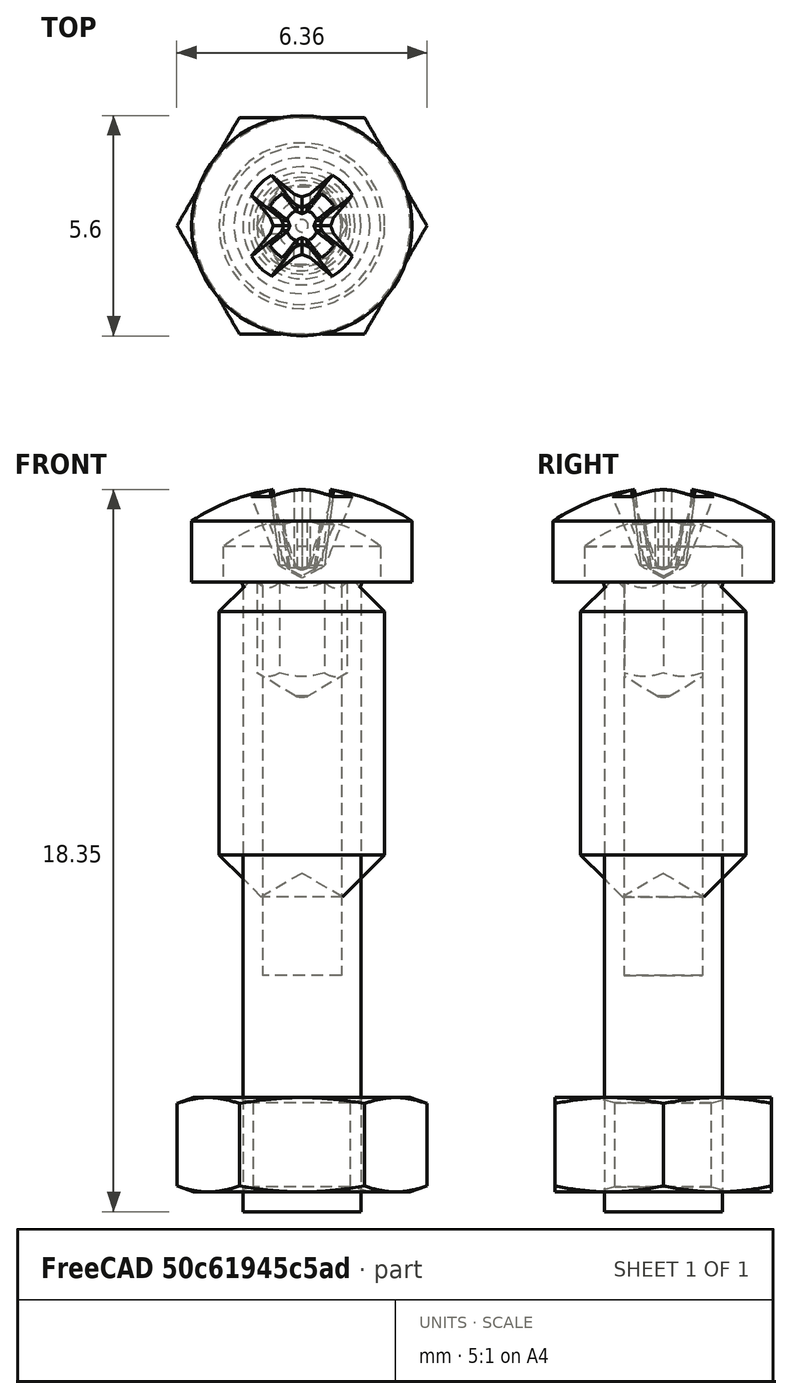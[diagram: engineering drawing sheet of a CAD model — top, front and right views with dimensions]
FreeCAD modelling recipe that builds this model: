
FCSTD DOCUMENT  (FreeCAD 0.19R24367 (Git))
Label: AssemblySteeringL
License: All rights reserved
LicenseURL: http://en.wikipedia.org/wiki/All_rights_reserved
objects: App::Link×16, PartDesign::CoordinateSystem×7, Part::FeaturePython×4, App::Part×4, App::DocumentObjectGroup×3, App::FeaturePython×1
note: 11 computed .brp shape members not serialized (recipe doc carries the construction recipe); baked Part::Feature solids carry a one-line shape summary decoded from their .brp
EXTERNAL_REF file=parts/SteeringKnuckle.FCStd obj=LCS_0001
EXTERNAL_REF file=parts/SteeringKnuckle.FCStd obj=SteeringKnuckleBottomL
EXTERNAL_REF file=parts/Servo.FCStd obj=LCS_1
EXTERNAL_REF file=parts/SteeringKnuckle.FCStd obj=LCS_2
EXTERNAL_REF file=parts/Servo.FCStd obj=Assembly
EXTERNAL_REF file=parts/SteeringKnuckle.FCStd obj=LCS_1
EXTERNAL_REF file=parts/SteeringKnuckle.FCStd obj=LCS_3
EXTERNAL_REF file=parts/SteeringKnuckle.FCStd obj=SteeringKnuckleTop
EXTERNAL_REF file=parts/SteeringKnuckle.FCStd obj=LCS_Screw01
EXTERNAL_REF file=parts/SteeringKnuckle.FCStd obj=LCS_Screw02
EXTERNAL_REF file=parts/SteeringKnuckle.FCStd obj=LCS_Screw03
EXTERNAL_REF file=parts/SteeringKnuckle.FCStd obj=LCS_Screw04
EXTERNAL_REF file=parts/Servo.FCStd obj=LCS_PlateTop
EXTERNAL_REF file=parts/ServoCoupler.FCStd obj=LCS_Bottom
EXTERNAL_REF file=parts/ServoCoupler.FCStd obj=ServoCoupler
EXTERNAL_REF file=parts/FixedRing.FCStd obj=LCS_Bottom
EXTERNAL_REF file=parts/ServoCoupler.FCStd obj=LCS_Top
EXTERNAL_REF file=parts/FixedRing.FCStd obj=FixedRing
EXTERNAL_REF file=parts/ServoCoupler.FCStd obj=LCS_Hole03
EXTERNAL_REF file=parts/ServoCoupler.FCStd obj=LCS_Hole04
EXTERNAL_REF file=parts/ServoCoupler.FCStd obj=LCS_Hole01
EXTERNAL_REF file=parts/ServoCoupler.FCStd obj=LCS_Hole02
EXTERNAL_REF file=parts/BallBearing.FCStd obj=LCS_Top
EXTERNAL_REF file=parts/SteeringKnuckle.FCStd obj=LCS_BallBearing
EXTERNAL_REF file=parts/BallBearing.FCStd obj=BallBearing
EXTERNAL_REF file=parts/Shaft.FCStd obj=LCS_0
EXTERNAL_REF file=parts/Shaft.FCStd obj=Shaft
EXTERNAL_REF file=parts/SteeringKnuckle.FCStd obj=LCS_SurfaceBearing
EXTERNAL_REF file=parts/SurfaceBearing.FCStd obj=LCS_Bottom
EXTERNAL_REF file=parts/SurfaceBearing.FCStd obj=Model

FEATURE [PartDesign::CoordinateSystem] LCS_Origin
  AttacherType = Attacher::AttachEngine3D
  MapMode = 2
  Support = -> [X_Axis]
FEATURE [App::FeaturePython] Variables  # WARN: FeaturePython — macro-defined, semantics opaque (R4)
  Type = App::PropertyContainer
FEATURE [App::DocumentObjectGroup] Constraints
FEATURE [App::DocumentObjectGroup] Configurations
FEATURE [App::Link] SteeringKnuckleBottomL
  AssemblyType = Part::Link
  AttachedBy = #LCS_0001
  AttachedTo = Parent Assembly#LCS_Origin
  LinkedObject = -> <external parts/SteeringKnuckle.FCStd>#SteeringKnuckleBottomL
  SolverId = Asm4EE
  expr: Placement = LCS_Origin.Placement * AttachmentOffset * SteeringKnuckle#LCS_0001.Placement ^ -1
FEATURE [App::Link] AssemblyServo
  AttachedBy = #LCS_1
  AttachedTo = SteeringKnuckleBottomL#LCS_2
  LinkPlacement = pos=(3e-16,0,-8.3) rot=(0,0,1;0rad)
  LinkedObject = -> <external parts/Servo.FCStd>#Assembly
  Placement = pos=(3e-16,0,-8.3) rot=(0,0,1;0rad)
  SolverId = Asm4EE
  expr: Placement = SteeringKnuckleBottomL.Placement * SteeringKnuckle#LCS_2.Placement * AttachmentOffset * Servo#LCS_1.Placement ^ -1
FEATURE [App::Link] SteeringKnuckleTop
  AssemblyType = Part::Link
  AttachedBy = #LCS_1
  AttachedTo = SteeringKnuckleBottomL#LCS_3
  AttachmentOffset = pos=(0,0,0) rot=(0,0,1;3.14159rad)
  LinkedObject = -> <external parts/SteeringKnuckle.FCStd>#SteeringKnuckleTop
  SolverId = Asm4EE
  expr: Placement = SteeringKnuckleBottomL.Placement * SteeringKnuckle#LCS_3.Placement * AttachmentOffset * SteeringKnuckle#LCS_1.Placement ^ -1
FEATURE [PartDesign::CoordinateSystem] LCS_0
  AttacherType = Attacher::AttachEngine3D
  MapMode = 2
  Support = -> [X_Axis001]
FEATURE [Part::FeaturePython] Screw  label="M3x16-Screw"  # Fasteners workbench fastener (typed FeaturePython)
  diameter = 4
  invert = false
  length = 7
  lengthCustom = 16
  matchOuter = false
  offset = 0
  thread = false
  type = 34
FEATURE [Part::FeaturePython] Nut  label="M3-Nut"  # Fasteners workbench fastener (typed FeaturePython)
  Placement = pos=(0,0,-15.5) rot=(0,0,1;0rad)
  diameter = 4
  invert = false
  matchOuter = false
  offset = 0
  thread = false
  type = 7
FEATURE [PartDesign::CoordinateSystem] LCS_Screw
  AttacherType = Attacher::AttachEngine3D
  MapMode = 45
  Placement = pos=(0,-2e-16,0) rot=(0,1,0;3.14159rad)
  Support = -> [Screw]
FEATURE [App::Part] Fastener
  Group = -> [LCS_0,Screw,Nut,LCS_Screw]
  Origin = -> Origin001
FEATURE [App::Link] Fastener001
  AssemblyType = Part::Link
  AttachedBy = #LCS_Screw
  AttachedTo = SteeringKnuckleBottomL#LCS_Screw01
  LinkPlacement = pos=(-19.799,19.799,-3) rot=(0,-1,0;3.14159rad)
  LinkedObject = -> Fastener
  Placement = pos=(-19.799,19.799,-3) rot=(0,-1,0;3.14159rad)
  SolverId = Asm4EE
  expr: Placement = SteeringKnuckleBottomL.Placement * SteeringKnuckle#LCS_Screw01.Placement * AttachmentOffset * LCS_Screw.Placement ^ -1
FEATURE [App::Link] Fastener002
  AssemblyType = Part::Link
  AttachedBy = #LCS_Screw
  AttachedTo = SteeringKnuckleBottomL#LCS_Screw02
  LinkPlacement = pos=(-19.799,-19.799,-3) rot=(0,-1,0;3.14159rad)
  LinkedObject = -> Fastener
  Placement = pos=(-19.799,-19.799,-3) rot=(0,-1,0;3.14159rad)
  SolverId = Asm4EE
  expr: Placement = SteeringKnuckleBottomL.Placement * SteeringKnuckle#LCS_Screw02.Placement * AttachmentOffset * LCS_Screw.Placement ^ -1
FEATURE [App::Link] Fastener003
  AssemblyType = Part::Link
  AttachedBy = #LCS_Screw
  AttachedTo = SteeringKnuckleBottomL#LCS_Screw03
  LinkPlacement = pos=(19.799,-19.799,-3) rot=(0,-1,0;3.14159rad)
  LinkedObject = -> Fastener
  Placement = pos=(19.799,-19.799,-3) rot=(0,-1,0;3.14159rad)
  SolverId = Asm4EE
  expr: Placement = SteeringKnuckleBottomL.Placement * SteeringKnuckle#LCS_Screw03.Placement * AttachmentOffset * LCS_Screw.Placement ^ -1
FEATURE [App::Link] Fastener004
  AssemblyType = Part::Link
  AttachedBy = #LCS_Screw
  AttachedTo = SteeringKnuckleBottomL#LCS_Screw04
  LinkPlacement = pos=(19.799,19.799,-3) rot=(0,-1,0;3.14159rad)
  LinkedObject = -> Fastener
  Placement = pos=(19.799,19.799,-3) rot=(0,-1,0;3.14159rad)
  SolverId = Asm4EE
  expr: Placement = SteeringKnuckleBottomL.Placement * SteeringKnuckle#LCS_Screw04.Placement * AttachmentOffset * LCS_Screw.Placement ^ -1
FEATURE [App::Link] ServoCoupler
  AssemblyType = Part::Link
  AttachedBy = #LCS_Bottom
  AttachedTo = AssemblyServo#LCS_PlateTop
  LinkPlacement = pos=(7e-16,1.9e-15,-18.3) rot=(0,-1,0;3.14159rad)
  LinkedObject = -> <external parts/ServoCoupler.FCStd>#ServoCoupler
  Placement = pos=(7e-16,1.9e-15,-18.3) rot=(0,-1,0;3.14159rad)
  SolverId = Asm4EE
  expr: Placement = AssemblyServo.Placement * Servo#LCS_PlateTop.Placement * AttachmentOffset * ServoCoupler#LCS_Bottom.Placement ^ -1
FEATURE [App::Link] FixedRing
  AssemblyType = Part::Link
  AttachedBy = #LCS_Bottom
  AttachedTo = ServoCoupler#LCS_Top
  AttachmentOffset = pos=(0,0,1) rot=(0,0,1;0rad)
  LinkPlacement = pos=(-1.33e-14,2.3e-15,-26.3) rot=(0.382683,-0.92388,0;3.14159rad)
  LinkedObject = -> <external parts/FixedRing.FCStd>#FixedRing
  Placement = pos=(-1.33e-14,2.3e-15,-26.3) rot=(0.382683,-0.92388,0;3.14159rad)
  SolverId = Asm4EE
  expr: Placement = ServoCoupler.Placement * ServoCoupler#LCS_Top.Placement * AttachmentOffset * FixedRing#LCS_Bottom.Placement ^ -1
FEATURE [PartDesign::CoordinateSystem] LCS_0001
  AttacherType = Attacher::AttachEngine3D
  MapMode = 2
  Support = -> [X_Axis002]
FEATURE [Part::FeaturePython] Screw002  label="#8x8-Screw"  # Fasteners workbench fastener (typed FeaturePython)
  diameter = 8
  invert = false
  length = 27
  lengthCustom = 8
  matchOuter = false
  offset = 0
  thread = false
  type = 10
FEATURE [PartDesign::CoordinateSystem] LCS_1
  AttacherType = Attacher::AttachEngine3D
  MapMode = 45
  Placement = pos=(6.4e-15,1e-16,0) rot=(0,1,0;3.14159rad)
  Support = -> [Screw002]
FEATURE [App::Part] Screw001
  Group = -> [LCS_0001,Screw002,LCS_1]
  Origin = -> Origin002
FEATURE [App::Link] Screw001001
  AssemblyType = Part::Link
  AttachedBy = #LCS_1
  AttachedTo = ServoCoupler#LCS_Hole03
  LinkPlacement = pos=(7.70335,7.70335,-29.1452) rot=(0.678591,0.281096,0.678601;3.6896rad)
  LinkedObject = -> Screw001
  Placement = pos=(7.70335,7.70335,-29.1452) rot=(0.678591,0.281096,0.678601;3.6896rad)
  SolverId = Asm4EE
  expr: Placement = ServoCoupler.Placement * ServoCoupler#LCS_Hole03.Placement * AttachmentOffset * LCS_1.Placement ^ -1
FEATURE [App::Link] Screw001002
  AssemblyType = Part::Link
  AttachedBy = #LCS_1
  AttachedTo = ServoCoupler#LCS_Hole04
  LinkPlacement = pos=(-7.70335,7.70335,-29.1452) rot=(0.35739,0.862858,0.35742;4.5654rad)
  LinkedObject = -> Screw001
  Placement = pos=(-7.70335,7.70335,-29.1452) rot=(0.35739,0.862858,0.35742;4.5654rad)
  SolverId = Asm4EE
  expr: Placement = ServoCoupler.Placement * ServoCoupler#LCS_Hole04.Placement * AttachmentOffset * LCS_1.Placement ^ -1
FEATURE [PartDesign::CoordinateSystem] LCS_0002
  AttacherType = Attacher::AttachEngine3D
  MapMode = 2
  Support = -> [X_Axis003]
FEATURE [Part::FeaturePython] Screw001004  label="M2x10-Screw"  # Fasteners workbench fastener (typed FeaturePython)
  diameter = 2
  invert = false
  length = 5
  lengthCustom = 10
  matchOuter = false
  offset = 0
  thread = false
  type = 34
FEATURE [PartDesign::CoordinateSystem] LCS_2
  AttacherType = Attacher::AttachEngine3D
  MapMode = 45
  Placement = pos=(-9e-16,-3e-16,0) rot=(0,1,0;3.14159rad)
  Support = -> [Screw001004]
FEATURE [App::Part] Screw001003  label="Screw002"
  Group = -> [LCS_0002,Screw001004,LCS_2]
  Origin = -> Origin003
FEATURE [App::DocumentObjectGroup] Parts
  Group = -> [Fastener,Screw001,Screw001003]
FEATURE [App::Link] Screw002001
  AssemblyType = Part::Link
  AttachedBy = #LCS_2
  AttachedTo = ServoCoupler#LCS_Hole01
  LinkPlacement = pos=(-7,-2.48e-14,-25.3) rot=(0,-1,0;3.14159rad)
  LinkedObject = -> Screw001003
  Placement = pos=(-7,-2.48e-14,-25.3) rot=(0,-1,0;3.14159rad)
  SolverId = Asm4EE
  expr: Placement = ServoCoupler.Placement * ServoCoupler#LCS_Hole01.Placement * AttachmentOffset * LCS_2.Placement ^ -1
FEATURE [App::Link] Screw002002
  AssemblyType = Part::Link
  AttachedBy = #LCS_2
  AttachedTo = ServoCoupler#LCS_Hole02
  LinkPlacement = pos=(7,2.92e-14,-25.3) rot=(0,-1,0;3.14159rad)
  LinkedObject = -> Screw001003
  Placement = pos=(7,2.92e-14,-25.3) rot=(0,-1,0;3.14159rad)
  SolverId = Asm4EE
  expr: Placement = ServoCoupler.Placement * ServoCoupler#LCS_Hole02.Placement * AttachmentOffset * LCS_2.Placement ^ -1
FEATURE [App::Link] BallBearing
  AssemblyType = Part::Link
  AttachedBy = #LCS_Top
  AttachedTo = SteeringKnuckleBottomL#LCS_BallBearing
  LinkPlacement = pos=(1.59e-14,2e-16,-48) rot=(0,1,0;3.14159rad)
  LinkedObject = -> <external parts/BallBearing.FCStd>#BallBearing
  Placement = pos=(1.59e-14,2e-16,-48) rot=(0,1,0;3.14159rad)
  SolverId = Asm4EE
  expr: Placement = SteeringKnuckleBottomL.Placement * SteeringKnuckle#LCS_BallBearing.Placement * AttachmentOffset * BallBearing#LCS_Top.Placement ^ -1
FEATURE [App::Link] Shaft
  AssemblyType = Part::Link
  AttachedBy = #LCS_0
  AttachedTo = FixedRing#LCS_Bottom
  LinkPlacement = pos=(-1.3e-14,2e-15,-26.3) rot=(0,-1,0;3.14159rad)
  LinkedObject = -> <external parts/Shaft.FCStd>#Shaft
  Placement = pos=(-1.3e-14,2e-15,-26.3) rot=(0,-1,0;3.14159rad)
  SolverId = Asm4EE
  expr: Placement = FixedRing.Placement * FixedRing#LCS_Bottom.Placement * AttachmentOffset * Shaft#LCS_0.Placement ^ -1
FEATURE [App::Link] SurfaceBearing
  AttachedBy = #LCS_Bottom
  AttachedTo = SteeringKnuckleBottomL#LCS_SurfaceBearing
  LinkPlacement = pos=(2.16e-14,0,-58) rot=(0,1,0;3.14159rad)
  LinkedObject = -> <external parts/SurfaceBearing.FCStd>#Model
  Placement = pos=(2.16e-14,0,-58) rot=(0,1,0;3.14159rad)
  SolverId = Asm4EE
  expr: Placement = SteeringKnuckleBottomL.Placement * SteeringKnuckle#LCS_SurfaceBearing.Placement * AttachmentOffset * SurfaceBearing#LCS_Bottom.Placement ^ -1
FEATURE [App::Part] Assembly  label="AssemblySteeringL"
  AssemblyType = Part::Link
  Group = -> [LCS_Origin,Variables,Constraints,Configurations,SteeringKnuckleBottomL,AssemblyServo,SteeringKnuckleTop,Fastener001,Fastener002,Fastener003,Fastener004,ServoCoupler,FixedRing,Screw001001,Screw001002,Screw002001,Screw002002,BallBearing,Shaft,SurfaceBearing]
  Origin = -> Origin
  Type = Assembly

RESOLVED EXTERNAL PARTS (link-assembly join: the EXTERNAL_REF files above that resolve inside this repo's crawl, each included once):
---- part parts/FixedRing.FCStd = doc fcstd_d6dc02ef2379 ----
FCSTD DOCUMENT  (FreeCAD 0.19R24367 (Git))
Label: FixedRing
License: All rights reserved
LicenseURL: http://en.wikipedia.org/wiki/All_rights_reserved
objects: PartDesign::CoordinateSystem×5, Sketcher::SketchObject×4, PartDesign::Chamfer×4, App::DocumentObjectGroup×3, PartDesign::Pocket×3, App::Part×2, App::FeaturePython×1, PartDesign::Pad×1, PartDesign::Body×1
note: 26 computed .brp shape members not serialized (recipe doc carries the construction recipe); baked Part::Feature solids carry a one-line shape summary decoded from their .brp

FEATURE [PartDesign::CoordinateSystem] LCS_Origin
  AttacherType = Attacher::AttachEngine3D
  MapMode = 2
  Support = -> [X_Axis]
FEATURE [App::FeaturePython] Variables  # WARN: FeaturePython — macro-defined, semantics opaque (R4)
  Type = App::PropertyContainer
FEATURE [App::DocumentObjectGroup] Constraints
FEATURE [App::DocumentObjectGroup] Configurations
FEATURE [App::Part] Assembly
  AssemblyType = Part::Link
  Group = -> [LCS_Origin,Variables,Constraints,Configurations]
  Origin = -> Origin
  Type = Assembly
FEATURE [PartDesign::CoordinateSystem] LCS_0
  AttacherType = Attacher::AttachEngine3D
  MapMode = 2
  Support = -> [X_Axis001]
FEATURE [PartDesign::CoordinateSystem] LCS_0001
  AttacherType = Attacher::AttachEngine3D
  MapMode = 2
  Support = -> [X_Axis002]
FEATURE [Sketcher::SketchObject] Sketch
  FullyConstrained = true
  MapMode = 5
  Support = -> [XY_Plane002]
  sketch-geometry (1):
    g0: Circle CenterX=0 CenterY=0 CenterZ=0 NormalX=0 NormalY=0 NormalZ=1 AngleXU=0 Radius=6
  constraints (2):
    c: Coincident(g0,g-1)
    c: Diameter(g0) = 12
FEATURE [PartDesign::Pad] Pad
  Direction = (1,1,1)
  Length = 6
  Length2 = 100
  Profile = -> Sketch
  Type = 0
FEATURE [Sketcher::SketchObject] Sketch001
  FullyConstrained = true
  MapMode = 5
  Placement = pos=(0,0,6) rot=(0,0,1;0rad)
  Support = -> [Pad]
  sketch-geometry (1):
    g0: Circle CenterX=0 CenterY=0 CenterZ=0 NormalX=0 NormalY=0 NormalZ=1 AngleXU=0 Radius=3
  constraints (2):
    c: Coincident(g0,g-1)
    c: Diameter(g0) = 6
FEATURE [PartDesign::Pocket] Pocket
  BaseFeature = -> Pad
  Length = 5
  Length2 = 100
  Profile = -> Sketch001
  Type = 1
FEATURE [PartDesign::Chamfer] Chamfer
  Angle = 45
  Base = -> Pocket [Edge3]
  BaseFeature = -> Pocket
  ChamferType = 0
  FlipDirection = false
  Size = 1
  Size2 = 1
  SupportTransform = false
FEATURE [PartDesign::Chamfer] Chamfer001
  Angle = 45
  Base = -> Chamfer [Edge7]
  BaseFeature = -> Chamfer
  ChamferType = 0
  FlipDirection = false
  Size = 0.3
  Size2 = 1
  SupportTransform = false
FEATURE [PartDesign::Chamfer] Chamfer002
  Angle = 45
  Base = -> Chamfer001 [Edge10]
  BaseFeature = -> Chamfer001
  ChamferType = 0
  FlipDirection = false
  Size = 0.5
  Size2 = 1
  SupportTransform = false
FEATURE [PartDesign::Chamfer] Chamfer003
  Angle = 45
  Base = -> Chamfer002 [Edge8]
  BaseFeature = -> Chamfer002
  ChamferType = 0
  FlipDirection = false
  Size = 0.3
  Size2 = 1
  SupportTransform = false
FEATURE [Sketcher::SketchObject] Sketch002
  FullyConstrained = true
  MapMode = 5
  Placement = pos=(0,0,0) rot=(0.57735,0.57735,0.57735;2.0944rad)
  Support = -> [YZ_Plane002]
  sketch-geometry (1):
    g0: Circle CenterX=0 CenterY=2.8 CenterZ=0 NormalX=0 NormalY=0 NormalZ=1 AngleXU=0 Radius=2
  constraints (3):
    c: PointOnObject(g0,g-2)
    c: Diameter(g0) = 4
    c: DistanceY(g-1,g0) = 2.8
FEATURE [PartDesign::Pocket] Pocket001
  BaseFeature = -> Chamfer003
  Length = 5
  Length2 = 100
  Profile = -> Sketch002
  Type = 1
FEATURE [Sketcher::SketchObject] Sketch003
  FullyConstrained = true
  MapMode = 5
  Placement = pos=(0,0,0) rot=(1,0,0;1.5708rad)
  Support = -> [XZ_Plane002]
  sketch-geometry (1):
    g0: Circle CenterX=0 CenterY=2.8 CenterZ=0 NormalX=0 NormalY=0 NormalZ=1 AngleXU=0 Radius=2
  constraints (3):
    c: PointOnObject(g0,g-2)
    c: Diameter(g0) = 4
    c: DistanceY(g-1,g0) = 2.8
FEATURE [PartDesign::Pocket] Pocket002
  BaseFeature = -> Pocket001
  Length = 5
  Length2 = 100
  Profile = -> Sketch003
  Type = 1
FEATURE [PartDesign::Body] Body
  Group = -> [LCS_0001,Sketch,Pad,Sketch001,Pocket,Chamfer,Chamfer001,Chamfer002,Chamfer003,Sketch002,Pocket001,Sketch003,Pocket002]
  Origin = -> Origin002
  Tip = -> Pocket002
FEATURE [PartDesign::CoordinateSystem] LCS_Top
  AttacherType = Attacher::AttachEngine3D
  MapMode = 45
  Placement = pos=(-2.7e-15,-7e-16,6) rot=(0,0,1;0rad)
  Support = -> [Pocket002]
FEATURE [PartDesign::CoordinateSystem] LCS_Bottom
  AttacherType = Attacher::AttachEngine3D
  AttachmentOffset = pos=(0,0,0) rot=(0,0,1;0.785398rad)
  MapMode = 45
  Placement = pos=(0,-4e-16,0) rot=(0,0,1;0.785398rad)
  Support = -> [Pocket002]
FEATURE [App::Part] FixedRing
  Group = -> [LCS_0,Body,LCS_Top,LCS_Bottom]
  Origin = -> Origin001
FEATURE [App::DocumentObjectGroup] Parts
  Group = -> [FixedRing]
---- part parts/Servo.FCStd = doc fcstd_7c5f7352c85d ----
FCSTD DOCUMENT  (FreeCAD 0.19R24367 (Git))
Label: Servo
License: All rights reserved
LicenseURL: http://en.wikipedia.org/wiki/All_rights_reserved
objects: Sketcher::SketchObject×15, PartDesign::CoordinateSystem×13, PartDesign::Fillet×12, PartDesign::Pad×10, App::Link×6, PartDesign::Chamfer×5, PartDesign::Pocket×5, App::Part×4, PartDesign::Body×3, App::DocumentObjectGroup×3, Part::FeaturePython×2, PartDesign::SubShapeBinder×2, App::FeaturePython×1, PartDesign::PolarPattern×1, PartDesign::Mirrored×1
note: 101 computed .brp shape members not serialized (recipe doc carries the construction recipe); baked Part::Feature solids carry a one-line shape summary decoded from their .brp

FEATURE [PartDesign::CoordinateSystem] LCS_0
  AttacherType = Attacher::AttachEngine3D
  MapMode = 2
  Support = -> [X_Axis]
FEATURE [PartDesign::CoordinateSystem] LCS_0001
  AttacherType = Attacher::AttachEngine3D
  MapMode = 2
  Support = -> [X_Axis001]
FEATURE [Sketcher::SketchObject] Sketch
  FullyConstrained = true
  MapMode = 5
  Support = -> [XY_Plane001]
  sketch-geometry (4):
    g0: LineSegment StartX=-10 StartY=10 StartZ=0 EndX=30 EndY=10 EndZ=0
    g1: LineSegment StartX=30 StartY=10 StartZ=0 EndX=30 EndY=-10 EndZ=0
    g2: LineSegment StartX=30 StartY=-10 StartZ=0 EndX=-10 EndY=-10 EndZ=0
    g3: LineSegment StartX=-10 StartY=-10 StartZ=0 EndX=-10 EndY=10 EndZ=0
  constraints (11):
    c: Coincident(g0,g1)
    c: Coincident(g1,g2)
    c: Coincident(g2,g3)
    c: Coincident(g3,g0)
    c: Horizontal(g0)
    c: Horizontal(g2)
    c: Vertical(g1)
    c: Symmetric(g0,g2,g-1)
    c: Distance(g0) = 40
    c: Distance(g1) = 20
    c: DistanceX(g0,g-1) = 10
FEATURE [PartDesign::Pad] Pad
  Direction = (1,1,1)
  Length = 36.8
  Length2 = 100
  Profile = -> Sketch
  Type = 0
FEATURE [PartDesign::Chamfer] Chamfer
  Angle = 45
  Base = -> Pad [Edge4]
  BaseFeature = -> Pad
  ChamferType = 0
  FlipDirection = false
  Size = 2
  Size2 = 1
  SupportTransform = false
FEATURE [PartDesign::Chamfer] Chamfer001
  Angle = 45
  Base = -> Chamfer [Edge15]
  BaseFeature = -> Chamfer
  ChamferType = 0
  FlipDirection = false
  Size = 2
  Size2 = 1
  SupportTransform = false
FEATURE [PartDesign::Chamfer] Chamfer002
  Angle = 45
  Base = -> Chamfer001 [Edge7]
  BaseFeature = -> Chamfer001
  ChamferType = 0
  FlipDirection = false
  Size = 2
  Size2 = 1
  SupportTransform = false
FEATURE [PartDesign::Chamfer] Chamfer003
  Angle = 45
  Base = -> Chamfer002 [Edge3]
  BaseFeature = -> Chamfer002
  ChamferType = 0
  FlipDirection = false
  Size = 2
  Size2 = 1
  SupportTransform = false
FEATURE [Sketcher::SketchObject] Sketch001
  ExternalGeometry = -> [Chamfer003]
  FullyConstrained = true
  MapMode = 5
  Placement = pos=(0,0,36.8) rot=(0,0,1;0rad)
  Support = -> [Chamfer003]
  sketch-geometry (4):
    g0: Circle CenterX=-8 CenterY=8 CenterZ=0 NormalX=0 NormalY=0 NormalZ=1 AngleXU=0 Radius=2.82843
    g1: Circle CenterX=28 CenterY=8 CenterZ=0 NormalX=0 NormalY=0 NormalZ=1 AngleXU=0 Radius=2.82843
    g2: Circle CenterX=28 CenterY=-8 CenterZ=0 NormalX=0 NormalY=0 NormalZ=1 AngleXU=0 Radius=2.82843
    g3: Circle CenterX=-8 CenterY=-8 CenterZ=0 NormalX=0 NormalY=0 NormalZ=1 AngleXU=0 Radius=2.82843
  constraints (8):
    c: Coincident(g0,g-3)
    c: PointOnObject(g-7,g0)
    c: Coincident(g1,g-6)
    c: Coincident(g2,g-5)
    c: Coincident(g3,g-4)
    c: PointOnObject(g-8,g1)
    c: PointOnObject(g-9,g2)
    c: PointOnObject(g-10,g3)
FEATURE [PartDesign::Pocket] Pocket
  BaseFeature = -> Chamfer003
  Length = 1.5
  Length2 = 100
  Profile = -> Sketch001
  Type = 0
FEATURE [Sketcher::SketchObject] Sketch002
  ExternalGeometry = -> [Pocket]
  FullyConstrained = true
  MapMode = 5
  Placement = pos=(0,0,36.8) rot=(0,0,1;0rad)
  Support = -> [Pocket]
  sketch-geometry (8):
    g0: LineSegment StartX=-8 StartY=8 StartZ=0 EndX=28 EndY=8 EndZ=0
    g1: LineSegment StartX=28 StartY=8 StartZ=0 EndX=28 EndY=-8 EndZ=0
    g2: LineSegment StartX=28 StartY=-8 StartZ=0 EndX=-8 EndY=-8 EndZ=0
    g3: LineSegment StartX=-8 StartY=-8 StartZ=0 EndX=-8 EndY=8 EndZ=0
    g4: Circle CenterX=-8 CenterY=8 CenterZ=0 NormalX=0 NormalY=0 NormalZ=1 AngleXU=0 Radius=1
    g5: Circle CenterX=28 CenterY=8 CenterZ=0 NormalX=0 NormalY=0 NormalZ=1 AngleXU=0 Radius=1
    g6: Circle CenterX=-8 CenterY=-8 CenterZ=0 NormalX=0 NormalY=0 NormalZ=1 AngleXU=0 Radius=1
    g7: Circle CenterX=28 CenterY=-8 CenterZ=0 NormalX=0 NormalY=0 NormalZ=1 AngleXU=0 Radius=1
  constraints (19):
    c: Coincident(g0,g1)
    c: Coincident(g1,g2)
    c: Coincident(g2,g3)
    c: Coincident(g3,g0)
    c: Horizontal(g0)
    c: Horizontal(g2)
    c: Vertical(g1)
    c: Symmetric(g0,g2,g-1)
    c: DistanceY(g-3,g0) = 0
    c: DistanceX(g0,g-4) = 0
    c: DistanceX(g-5,g2) = 0
    c: Coincident(g4,g0)
    c: Coincident(g5,g0)
    c: Coincident(g6,g2)
    c: Coincident(g7,g1)
    c: Diameter(g4) = 2
    c: Diameter(g5) = 2
    c: Diameter(g6) = 2
    c: Diameter(g7) = 2
FEATURE [PartDesign::Pocket] Pocket001
  BaseFeature = -> Pocket
  Length = 5
  Length2 = 100
  Profile = -> Sketch002
  Type = 0
FEATURE [Sketcher::SketchObject] Sketch003
  FullyConstrained = true
  MapMode = 5
  Placement = pos=(0,0,0) rot=(1,0,0;3.14159rad)
  Support = -> [Pocket001]
  sketch-geometry (1):
    g0: Circle CenterX=0 CenterY=0 CenterZ=0 NormalX=0 NormalY=0 NormalZ=1 AngleXU=0 Radius=10
  constraints (2):
    c: Coincident(g0,g-1)
    c: Diameter(g0) = 20
FEATURE [PartDesign::Pad] Pad001
  BaseFeature = -> Pocket001
  Direction = (1,1,1)
  Length = 2
  Length2 = 100
  Profile = -> Sketch003
  Refine = true
  Type = 0
FEATURE [Sketcher::SketchObject] Sketch004
  FullyConstrained = true
  MapMode = 5
  Placement = pos=(0,0,0) rot=(1,0,0;3.14159rad)
  Support = -> [Pad001]
  sketch-geometry (4):
    g0: LineSegment StartX=0 StartY=10 StartZ=0 EndX=24 EndY=10 EndZ=0
    g1: LineSegment StartX=24 StartY=10 StartZ=0 EndX=24 EndY=-10 EndZ=0
    g2: LineSegment StartX=24 StartY=-10 StartZ=0 EndX=0 EndY=-10 EndZ=0
    g3: LineSegment StartX=0 StartY=-10 StartZ=0 EndX=0 EndY=10 EndZ=0
  constraints (11):
    c: Coincident(g0,g1)
    c: Coincident(g1,g2)
    c: Coincident(g2,g3)
    c: Coincident(g3,g0)
    c: Horizontal(g0)
    c: Horizontal(g2)
    c: Vertical(g1)
    c: Symmetric(g0,g2,g-1)
    c: Distance(g0) = 24
    c: Distance(g3) = 20
    c: DistanceX(g0,g-1) = 0
FEATURE [PartDesign::Pad] Pad002
  BaseFeature = -> Pad001
  Direction = (1,1,1)
  Length = 2
  Length2 = 100
  Profile = -> Sketch004
  Refine = true
  Type = 0
FEATURE [Sketcher::SketchObject] Sketch005
  ExternalGeometry = -> [Pad002]
  FullyConstrained = true
  MapMode = 5
  Placement = pos=(0,0,0) rot=(1,0,0;3.14159rad)
  Support = -> [Pad002]
  sketch-geometry (2):
    g0: ArcOfCircle CenterX=23 CenterY=0 CenterZ=0 NormalX=0 NormalY=0 NormalZ=1 AngleXU=0 Radius=4.60977 StartAngle=4.93106 EndAngle=7.63531
    g1: LineSegment StartX=24 StartY=4.5 StartZ=0 EndX=24 EndY=-4.5 EndZ=0
  constraints (7):
    c: PointOnObject(g0,g-1)
    c: PointOnObject(g0,g-3)
    c: PointOnObject(g0,g-3)
    c: DistanceY(g0,g0) = 9
    c: DistanceX(g0,g-3) = 1
    c: Coincident(g1,g0)
    c: Coincident(g1,g0)
FEATURE [PartDesign::Pad] Pad003
  BaseFeature = -> Pad002
  Direction = (1,1,1)
  Length = 2
  Length2 = 100
  Profile = -> Sketch005
  Refine = true
  Type = 0
FEATURE [PartDesign::Fillet] Fillet
  Base = -> Pad003 [Edge40]
  BaseFeature = -> Pad003
  Radius = 1
  SupportTransform = false
FEATURE [PartDesign::Fillet] Fillet001
  Base = -> Fillet [Edge44]
  BaseFeature = -> Fillet
  Radius = 1
  SupportTransform = false
FEATURE [PartDesign::Fillet] Fillet002
  Base = -> Fillet001 [Edge53]
  BaseFeature = -> Fillet001
  Radius = 1
  SupportTransform = false
FEATURE [PartDesign::Fillet] Fillet003
  Base = -> Fillet002 [Edge65]
  BaseFeature = -> Fillet002
  Radius = 1
  SupportTransform = false
FEATURE [PartDesign::Fillet] Fillet004
  Base = -> Fillet003 [Face28]
  BaseFeature = -> Fillet003
  Radius = 0.5
  SupportTransform = false
FEATURE [Sketcher::SketchObject] Sketch006
  FullyConstrained = true
  MapMode = 5
  Placement = pos=(0,0,-2) rot=(1,0,0;3.14159rad)
  Support = -> [Fillet004]
  sketch-geometry (1):
    g0: Circle CenterX=0 CenterY=0 CenterZ=0 NormalX=0 NormalY=0 NormalZ=1 AngleXU=0 Radius=6.5
  constraints (2):
    c: Coincident(g0,g-1)
    c: Diameter(g0) = 13
FEATURE [PartDesign::Pad] Pad004
  BaseFeature = -> Fillet004
  Direction = (1,1,1)
  Length = 2
  Length2 = 100
  Profile = -> Sketch006
  Type = 0
FEATURE [PartDesign::Fillet] Fillet005
  Base = -> Pad004 [Edge96]
  BaseFeature = -> Pad004
  Radius = 0.5
  SupportTransform = false
FEATURE [Part::FeaturePython] involutegear  # WARN: FeaturePython — macro-defined, semantics opaque (R4)
  AttacherType = Attacher::AttachEngine3D
  Placement = pos=(0,0,-8) rot=(0,0,1;0rad)
  backlash = 0
  beta = 0
  clearance = 0.15
  da = 5.6
  df = 3.88
  double_helix = false
  dw = 4.8
  head = 0
  height = 4
  module = 0.4
  numpoints = 6
  pressure_angle = 20
  properties_from_tool = false
  reversed_backlash = false
  shift = 0
  simple = false
  teeth = 12
  transverse_pitch = 1.25664
  undercut = false
  version = 0.0.3
FEATURE [Part::FeaturePython] Screw  label="M2x20-Screw"  # Fasteners workbench fastener (typed FeaturePython)
  Placement = pos=(-8,8,35.5) rot=(0,0,1;0rad)
  diameter = 2
  invert = false
  length = 9
  lengthCustom = 20
  matchOuter = false
  offset = 0
  thread = false
  type = 34
FEATURE [App::Link] Link  label="M2x20-Screw001"
  LinkPlacement = pos=(28,8,35.5) rot=(0,0,1;0rad)
  LinkedObject = -> Screw
  Placement = pos=(28,8,35.5) rot=(0,0,1;0rad)
FEATURE [App::Link] Link001  label="M2x20-Screw002"
  LinkPlacement = pos=(-8,-8,35.5) rot=(0,0,1;0rad)
  LinkedObject = -> Screw
  Placement = pos=(-8,-8,35.5) rot=(0,0,1;0rad)
FEATURE [App::Link] Link002  label="M2x20-Screw003"
  LinkPlacement = pos=(28,-8.00001,35.5) rot=(0,0,1;0rad)
  LinkedObject = -> Screw
  Placement = pos=(28,-8.00001,35.5) rot=(0,0,1;0rad)
FEATURE [Sketcher::SketchObject] Sketch007
  ExternalGeometry = -> [Fillet005]
  FullyConstrained = true
  MapMode = 5
  Placement = pos=(-10,0,0) rot=(0.57735,-0.57735,-0.57735;2.0944rad)
  Support = -> [Fillet005]
  sketch-geometry (4):
    g0: LineSegment StartX=-3.5 StartY=33.8 StartZ=0 EndX=3.5 EndY=33.8 EndZ=0
    g1: LineSegment StartX=3.5 StartY=33.8 StartZ=0 EndX=3.5 EndY=29.8 EndZ=0
    g2: LineSegment StartX=3.5 StartY=29.8 StartZ=0 EndX=-3.5 EndY=29.8 EndZ=0
    g3: LineSegment StartX=-3.5 StartY=29.8 StartZ=0 EndX=-3.5 EndY=33.8 EndZ=0
  constraints (11):
    c: Coincident(g0,g1)
    c: Coincident(g1,g2)
    c: Coincident(g2,g3)
    c: Coincident(g3,g0)
    c: Horizontal(g2)
    c: Vertical(g1)
    c: Vertical(g3)
    c: Symmetric(g0,g0,g-2)
    c: DistanceY(g2,g-3) = 7
    c: Distance(g1) = 4
    c: Distance(g0) = 7
FEATURE [PartDesign::Pad] Pad005
  BaseFeature = -> Fillet005
  Direction = (1,1,1)
  Length = 5
  Length2 = 100
  Profile = -> Sketch007
  Type = 0
FEATURE [PartDesign::Fillet] Fillet006
  Base = -> Pad005 [Face47]
  BaseFeature = -> Pad005
  Radius = 0.5
  SupportTransform = false
FEATURE [PartDesign::Body] Body
  Group = -> [LCS_0001,Sketch,Pad,Chamfer,Chamfer001,Chamfer002,Chamfer003,Sketch001,Pocket,Sketch002,Pocket001,Sketch003,Pad001,Sketch004,Pad002,Sketch005,Pad003,Fillet,Fillet001,Fillet002,Fillet003,Fillet004,Sketch006,Pad004,Fillet005,Sketch007,Pad005,Fillet006]
  Origin = -> Origin001
  Tip = -> Fillet006
FEATURE [PartDesign::CoordinateSystem] LCS_0002
  AttacherType = Attacher::AttachEngine3D
  MapMode = 2
  Support = -> [X_Axis002]
FEATURE [Sketcher::SketchObject] Sketch008
  FullyConstrained = true
  MapMode = 5
  Support = -> [XY_Plane002]
  sketch-geometry (4):
    g0: LineSegment StartX=-27 StartY=9.5 StartZ=0 EndX=27 EndY=9.5 EndZ=0
    g1: LineSegment StartX=27 StartY=9.5 StartZ=0 EndX=27 EndY=-9.5 EndZ=0
    g2: LineSegment StartX=27 StartY=-9.5 StartZ=0 EndX=-27 EndY=-9.5 EndZ=0
    g3: LineSegment StartX=-27 StartY=-9.5 StartZ=0 EndX=-27 EndY=9.5 EndZ=0
  constraints (11):
    c: Coincident(g0,g1)
    c: Coincident(g1,g2)
    c: Coincident(g2,g3)
    c: Coincident(g3,g0)
    c: Horizontal(g0)
    c: Horizontal(g2)
    c: Vertical(g1)
    c: Vertical(g3)
    c: Symmetric(g0,g1,g-1)
    c: Distance(g0) = 54
    c: Distance(g1) = 19
FEATURE [PartDesign::Pad] Pad006
  Direction = (1,1,1)
  Length = 2.5
  Length2 = 100
  Profile = -> Sketch008
  Type = 0
FEATURE [Sketcher::SketchObject] Sketch009
  FullyConstrained = true
  MapMode = 5
  Placement = pos=(0,0,2.5) rot=(0,0,1;0rad)
  Support = -> [Pad006]
  sketch-geometry (8):
    g0: LineSegment StartX=-24 StartY=5 StartZ=0 EndX=24 EndY=5 EndZ=0
    g1: LineSegment StartX=24 StartY=5 StartZ=0 EndX=24 EndY=-5 EndZ=0
    g2: LineSegment StartX=24 StartY=-5 StartZ=0 EndX=-24 EndY=-5 EndZ=0
    g3: LineSegment StartX=-24 StartY=-5 StartZ=0 EndX=-24 EndY=5 EndZ=0
    g4: Circle CenterX=-24 CenterY=5 CenterZ=0 NormalX=0 NormalY=0 NormalZ=1 AngleXU=0 Radius=2.5
    g5: Circle CenterX=24 CenterY=5 CenterZ=0 NormalX=0 NormalY=0 NormalZ=1 AngleXU=0 Radius=2.5
    g6: Circle CenterX=24 CenterY=-5 CenterZ=0 NormalX=0 NormalY=0 NormalZ=1 AngleXU=0 Radius=2.5
    g7: Circle CenterX=-24 CenterY=-5 CenterZ=0 NormalX=0 NormalY=0 NormalZ=1 AngleXU=0 Radius=2.5
  constraints (19):
    c: Coincident(g0,g1)
    c: Coincident(g1,g2)
    c: Coincident(g2,g3)
    c: Coincident(g3,g0)
    c: Horizontal(g0)
    c: Horizontal(g2)
    c: Vertical(g1)
    c: Vertical(g3)
    c: Symmetric(g0,g1,g-1)
    c: Distance(g0) = 48
    c: Distance(g1) = 10
    c: Coincident(g4,g0)
    c: Coincident(g5,g0)
    c: Coincident(g6,g1)
    c: Coincident(g7,g2)
    c: Diameter(g4) = 5
    c: Diameter(g5) = 5
    c: Diameter(g6) = 5
    c: Diameter(g7) = 5
FEATURE [PartDesign::Pocket] Pocket002
  BaseFeature = -> Pad006
  Length = 5
  Length2 = 100
  Profile = -> Sketch009
  Type = 1
FEATURE [PartDesign::Fillet] Fillet007
  Base = -> Pocket002 [Edge2]
  BaseFeature = -> Pocket002
  Radius = 2
  SupportTransform = false
FEATURE [PartDesign::Fillet] Fillet008
  Base = -> Fillet007 [Edge3]
  BaseFeature = -> Fillet007
  Radius = 2
  SupportTransform = false
FEATURE [PartDesign::Fillet] Fillet009
  Base = -> Fillet008 [Edge25]
  BaseFeature = -> Fillet008
  Radius = 2
  SupportTransform = false
FEATURE [PartDesign::Fillet] Fillet010
  Base = -> Fillet009 [Edge19]
  BaseFeature = -> Fillet009
  Radius = 2
  SupportTransform = false
FEATURE [Sketcher::SketchObject] Sketch010
  ExternalGeometry = -> [Fillet010]
  FullyConstrained = true
  MapMode = 5
  Placement = pos=(0,0,0) rot=(1,0,0;1.5708rad)
  Support = -> [XZ_Plane002]
  sketch-geometry (3):
    g0: LineSegment StartX=-27 StartY=0 StartZ=0 EndX=-19.6 EndY=0 EndZ=0
    g1: LineSegment StartX=-19.6 StartY=0 StartZ=0 EndX=-19.6 EndY=-2 EndZ=0
    g2: LineSegment StartX=-27 StartY=0 StartZ=0 EndX=-19.6 EndY=-2 EndZ=0
  constraints (9):
    c: PointOnObject(g0,g-1)
    c: Horizontal(g0)
    c: Vertical(g1)
    c: Coincident(g2,g0)
    c: Coincident(g2,g1)
    c: Distance(g1) = 2
    c: Distance(g0) = 7.4
    c: Coincident(g0,g1)
    c: DistanceX(g-3,g0) = 0
FEATURE [PartDesign::Pad] Pad007
  BaseFeature = -> Fillet010
  Direction = (1,1,1)
  Length = 1
  Length2 = 100
  Midplane = true
  Profile = -> Sketch010
  Type = 0
FEATURE [PartDesign::CoordinateSystem] LCS_Origin
  AttacherType = Attacher::AttachEngine3D
  MapMode = 2
  Support = -> [X_Axis003]
FEATURE [App::FeaturePython] Variables  # WARN: FeaturePython — macro-defined, semantics opaque (R4)
  Type = App::PropertyContainer
FEATURE [App::DocumentObjectGroup] Constraints
FEATURE [App::DocumentObjectGroup] Configurations
FEATURE [PartDesign::CoordinateSystem] LCS_0003
  AttacherType = Attacher::AttachEngine3D
  MapMode = 2
  Support = -> [X_Axis004]
FEATURE [PartDesign::CoordinateSystem] LCS_0004
  AttacherType = Attacher::AttachEngine3D
  MapMode = 2
  Support = -> [X_Axis005]
FEATURE [Sketcher::SketchObject] Sketch011
  FullyConstrained = true
  MapMode = 5
  Support = -> [XY_Plane005]
  sketch-geometry (1):
    g0: Circle CenterX=0 CenterY=0 CenterZ=0 NormalX=0 NormalY=0 NormalZ=1 AngleXU=0 Radius=10
  constraints (2):
    c: Coincident(g0,g-1)
    c: Diameter(g0) = 20
FEATURE [PartDesign::Pad] Pad008
  Direction = (1,1,1)
  Length = 2
  Length2 = 100
  Profile = -> Sketch011
  Type = 0
FEATURE [Sketcher::SketchObject] Sketch012
  FullyConstrained = true
  MapMode = 5
  Placement = pos=(0,0,0) rot=(1,0,0;3.14159rad)
  Support = -> [Pad008]
  sketch-geometry (1):
    g0: Circle CenterX=0 CenterY=0 CenterZ=0 NormalX=0 NormalY=0 NormalZ=1 AngleXU=0 Radius=4.5
  constraints (2):
    c: Coincident(g0,g-1)
    c: Diameter(g0) = 9
FEATURE [PartDesign::Pad] Pad009
  BaseFeature = -> Pad008
  Direction = (1,1,1)
  Length = 2.5
  Length2 = 100
  Profile = -> Sketch012
  Type = 0
FEATURE [Sketcher::SketchObject] Sketch013
  FullyConstrained = true
  MapMode = 5
  Placement = pos=(0,0,-2.5) rot=(1,0,0;3.14159rad)
  Support = -> [Pad009]
  sketch-geometry (1):
    g0: Circle CenterX=0 CenterY=0 CenterZ=0 NormalX=0 NormalY=0 NormalZ=1 AngleXU=0 Radius=2
  constraints (2):
    c: Coincident(g0,g-1)
    c: Diameter(g0) = 4
FEATURE [PartDesign::Pocket] Pocket003
  BaseFeature = -> Pad009
  Length = 5
  Length2 = 100
  Profile = -> Sketch013
  Type = 1
FEATURE [PartDesign::Chamfer] Chamfer004
  Angle = 45
  Base = -> Pocket003 [Edge8]
  BaseFeature = -> Pocket003
  ChamferType = 0
  FlipDirection = false
  Size = 0.5
  Size2 = 1
  SupportTransform = false
FEATURE [PartDesign::Fillet] Fillet011
  Base = -> Chamfer004 [Edge7]
  BaseFeature = -> Chamfer004
  Radius = 0.5
  SupportTransform = false
FEATURE [Sketcher::SketchObject] Sketch014
  FullyConstrained = true
  MapMode = 5
  Placement = pos=(0,0,0) rot=(1,0,0;3.14159rad)
  Support = -> [Fillet011]
  sketch-geometry (2):
    g0: Circle CenterX=0 CenterY=0 CenterZ=0 NormalX=0 NormalY=0 NormalZ=1 AngleXU=0 Radius=7
    g1: Circle CenterX=7 CenterY=0 CenterZ=0 NormalX=0 NormalY=0 NormalZ=1 AngleXU=0 Radius=1.5
  constraints (5):
    c: Coincident(g0,g-1)
    c: Diameter(g0) = 14
    c: PointOnObject(g1,g0)
    c: Diameter(g1) = 3
    c: PointOnObject(g1,g-1)
FEATURE [PartDesign::Pocket] Pocket004
  BaseFeature = -> Fillet011
  Length = 5
  Length2 = 100
  Profile = -> Sketch014
  Type = 1
FEATURE [PartDesign::PolarPattern] PolarPattern
  Angle = 360
  Axis = -> Sketch014 [N_Axis]
  BaseFeature = -> Pocket004
  Occurrences = 4
  Originals = -> [Pocket004]
FEATURE [PartDesign::Body] Body_3
  Group = -> [LCS_0004,Sketch011,Pad008,Sketch012,Pad009,Sketch013,Pocket003,Chamfer004,Fillet011,Sketch014,Pocket004,PolarPattern]
  Origin = -> Origin005
  Tip = -> PolarPattern
FEATURE [PartDesign::CoordinateSystem] LCS_Bottom
  AttacherType = Attacher::AttachEngine3D
  MapMode = 45
  Placement = pos=(10,-3e-16,36.8) rot=(0.707107,-0.707107,0;3.14159rad)
  Support = -> [Fillet006]
FEATURE [PartDesign::Mirrored] Mirrored
  BaseFeature = -> Pad007
  MirrorPlane = -> Sketch010 [V_Axis]
  Originals = -> [Pad007]
FEATURE [PartDesign::Body] Body_2  label="Body001"
  Group = -> [LCS_0002,Sketch008,Pad006,Sketch009,Pocket002,Fillet007,Fillet008,Fillet009,Fillet010,Sketch010,Pad007,Mirrored]
  Origin = -> Origin002
  Tip = -> Mirrored
FEATURE [PartDesign::CoordinateSystem] LCS_Bottom001
  AttacherType = Attacher::AttachEngine3D
  MapMode = 45
  Placement = pos=(-6e-16,-1e-16,2.5) rot=(0.707107,-0.707107,0;3.14159rad)
  Support = -> [Mirrored]
FEATURE [PartDesign::CoordinateSystem] LCS_Top
  AttacherType = Attacher::AttachEngine3D
  MapMode = 45
  Placement = pos=(2e-16,-2e-16,0) rot=(-0.707107,0.707107,0;3.14159rad)
  Support = -> [Mirrored]
FEATURE [App::Part] Hang
  Group = -> [Body_2,LCS_Bottom001,LCS_Top]
  Origin = -> Origin006
FEATURE [App::Link] Servo001
  AssemblyType = Part::Link
  AttachedBy = #LCS_0
  AttachedTo = Parent Assembly#LCS_Origin
  LinkedObject = -> Servo
  SolverId = Asm4EE
  expr: Placement = LCS_Origin.Placement * AttachmentOffset * LCS_0.Placement ^ -1
FEATURE [App::Link] Hang001
  AssemblyType = Part::Link
  AttachedBy = #LCS_Bottom001
  AttachedTo = Servo001#LCS_Bottom
  AttachmentOffset = pos=(0,0,29) rot=(0,0,1;0rad)
  LinkPlacement = pos=(10,-1e-16,5.3) rot=(0,0,1;0rad)
  LinkedObject = -> Hang
  Placement = pos=(10,-1e-16,5.3) rot=(0,0,1;0rad)
  SolverId = Asm4EE
  expr: Placement = Servo001.Placement * LCS_Bottom.Placement * AttachmentOffset * LCS_Bottom001.Placement ^ -1
FEATURE [PartDesign::CoordinateSystem] LCS_Gear001
  AttacherType = Attacher::AttachEngine3D
  MapMode = 11
  Placement = pos=(0,0,0) rot=(0,0,1;1.5708rad)
  Support = -> [PolarPattern]
FEATURE [App::Part] ServoWheel
  Group = -> [LCS_0003,Body_3,LCS_Gear001]
  Origin = -> Origin004
FEATURE [PartDesign::CoordinateSystem] LCS_Gear
  AttacherType = Attacher::AttachEngine3D
  MapMode = 45
  Placement = pos=(-5e-16,-5e-16,-8) rot=(0,1,0;3.14159rad)
  Support = -> [involutegear]
FEATURE [App::Part] Servo
  Group = -> [LCS_0,Body,involutegear,Screw,Link,Link001,Link002,LCS_Bottom,LCS_Gear]
  Origin = -> Origin
FEATURE [App::DocumentObjectGroup] Parts
  Group = -> [Servo,ServoWheel,Hang]
FEATURE [App::Link] ServoWheel001
  AssemblyType = Part::Link
  AttachedBy = #LCS_Gear001
  AttachedTo = Servo001#LCS_Gear
  LinkPlacement = pos=(-5e-16,-5e-16,-8) rot=(-0.707107,0.707107,0;3.14159rad)
  LinkedObject = -> ServoWheel
  Placement = pos=(-5e-16,-5e-16,-8) rot=(-0.707107,0.707107,0;3.14159rad)
  SolverId = Asm4EE
  expr: Placement = Servo001.Placement * LCS_Gear.Placement * AttachmentOffset * LCS_Gear001.Placement ^ -1
FEATURE [PartDesign::SubShapeBinder] ShapeBinder
  BindMode = 0
  ClaimChildren = false
  Context = -> Assembly [ShapeBinder.]
  Fuse = false
  MakeFace = false
  PartialLoad = false
  Relative = true
  Support = -> [Hang001[Body_2.Mirrored.Face1]]
  _Version = 2
FEATURE [PartDesign::CoordinateSystem] LCS_1  label="LCS_ServoTop"
  AttacherType = Attacher::AttachEngine3D
  AttachmentOffset = pos=(0,0,0) rot=(0,0,1;3.14159rad)
  MapMode = 5
  Placement = pos=(-5e-16,-5e-16,5.3) rot=(0,-1,0;3.14159rad)
  Support = -> [ShapeBinder]
FEATURE [PartDesign::SubShapeBinder] ShapeBinder001
  BindMode = 0
  ClaimChildren = false
  Context = -> Assembly [ShapeBinder001.]
  Fuse = false
  MakeFace = false
  PartialLoad = false
  Relative = true
  Support = -> [ServoWheel001[Body_3.PolarPattern.Face7]]
  _Version = 2
FEATURE [PartDesign::CoordinateSystem] LCS_PlateTop
  AttacherType = Attacher::AttachEngine3D
  MapMode = 45
  Placement = pos=(0,9e-16,-10) rot=(0,1,0;3.14159rad)
  Support = -> [ShapeBinder001]
FEATURE [App::Part] Assembly  label="AssemblyServo"
  AssemblyType = Part::Link
  Group = -> [LCS_Origin,Variables,Constraints,Configurations,Servo001,Hang001,ServoWheel001,ShapeBinder,LCS_1,ShapeBinder001,LCS_PlateTop]
  Origin = -> Origin003
  Type = Assembly
---- part parts/ServoCoupler.FCStd = doc fcstd_f0e325bff017 ----
FCSTD DOCUMENT  (FreeCAD 0.19R24367 (Git))
Label: ServoCoupler
License: All rights reserved
LicenseURL: http://en.wikipedia.org/wiki/All_rights_reserved
objects: PartDesign::CoordinateSystem×8, Sketcher::SketchObject×5, PartDesign::Pocket×3, App::DocumentObjectGroup×3, PartDesign::PolarPattern×2, App::Part×2, App::Link×2, PartDesign::Pad×1, PartDesign::Hole×1, PartDesign::Plane×1, PartDesign::Body×1, App::FeaturePython×1
note: 27 computed .brp shape members not serialized (recipe doc carries the construction recipe); baked Part::Feature solids carry a one-line shape summary decoded from their .brp
EXTERNAL_REF file=FixedRing.FCStd obj=LCS_Bottom
EXTERNAL_REF file=FixedRing.FCStd obj=FixedRing

FEATURE [Sketcher::SketchObject] Sketch004
  FullyConstrained = true
  MapMode = 5
  Support = -> [XY_Plane001]
  sketch-geometry (1):
    g0: Circle CenterX=0 CenterY=0 CenterZ=0 NormalX=0 NormalY=0 NormalZ=1 AngleXU=0 Radius=11
  constraints (2):
    c: Coincident(g0,g-1)
    c: Diameter(g0) = 22
FEATURE [PartDesign::Pad] Pad001
  Direction = (1,1,1)
  Length = 15
  Length2 = 100
  Profile = -> Sketch004
  Type = 0
FEATURE [Sketcher::SketchObject] Sketch005
  FullyConstrained = true
  MapMode = 5
  Placement = pos=(0,0,15) rot=(0,0,1;0rad)
  Support = -> [Pad001]
  sketch-geometry (1):
    g0: Circle CenterX=0 CenterY=0 CenterZ=0 NormalX=0 NormalY=0 NormalZ=1 AngleXU=0 Radius=6.15
  constraints (2):
    c: Coincident(g0,g-1)
    c: Diameter(g0) = 12.3
FEATURE [PartDesign::Pocket] Pocket002
  BaseFeature = -> Pad001
  Length = 8
  Length2 = 100
  Profile = -> Sketch005
  Type = 0
FEATURE [Sketcher::SketchObject] Sketch006
  FullyConstrained = true
  MapMode = 5
  Placement = pos=(0,0,15) rot=(0,0,1;0rad)
  Support = -> [Pocket002]
  sketch-geometry (1):
    g0: Circle CenterX=7 CenterY=0 CenterZ=0 NormalX=0 NormalY=0 NormalZ=1 AngleXU=0 Radius=2.75
  constraints (3):
    c: PointOnObject(g0,g-1)
    c: DistanceX(g-1,g0) = 7
    c: Diameter(g0) = 5.5
FEATURE [PartDesign::Hole] Hole001
  BaseFeature = -> Pocket002
  Depth = 8
  DepthType = 1
  Diameter = 2
  DrillForDepth = false
  DrillPoint = 0
  DrillPointAngle = 118
  HoleCutCountersinkAngle = 90
  HoleCutCustomValues = false
  HoleCutDepth = 8
  HoleCutDiameter = 5.5
  HoleCutType = 1
  ModelActualThread = false
  Profile = -> Sketch006
  Tapered = false
  TaperedAngle = 90
  ThreadAngle = 0
  ThreadClass = 0
  ThreadCutOffInner = 0
  ThreadCutOffOuter = 0
  ThreadDirection = 0
  ThreadFit = 0
  ThreadPitch = 0
  ThreadSize = 0
  ThreadType = 0
  Threaded = false
FEATURE [PartDesign::PolarPattern] PolarPattern001
  Angle = 360
  Axis = -> Sketch006 [N_Axis]
  BaseFeature = -> Hole001
  Occurrences = 2
  Originals = -> [Hole001]
FEATURE [PartDesign::Plane] DatumPlane
  AttachmentOffset = pos=(0,0,0) rot=(0.862856,0.357407,0.357407;1.71777rad)
  Length = 82.6027
  MapMode = 45
  Placement = pos=(-6.6e-15,-8e-16,8.84519) rot=(0.862856,0.357407,0.357407;1.71777rad)
  ResizeMode = 0
  Support = -> [PolarPattern001]
  Width = 61.8921
FEATURE [Sketcher::SketchObject] Sketch007
  FullyConstrained = true
  MapMode = 5
  Placement = pos=(-6.6e-15,-8e-16,8.84519) rot=(0.862856,0.357407,0.357407;1.71777rad)
  Support = -> [DatumPlane]
  sketch-geometry (1):
    g0: Circle CenterX=0 CenterY=2 CenterZ=0 NormalX=0 NormalY=0 NormalZ=1 AngleXU=0 Radius=2.15
  constraints (3):
    c: PointOnObject(g0,g-2)
    c: Diameter(g0) = 4.3
    c: DistanceY(g-1,g0) = 2
FEATURE [PartDesign::Pocket] Pocket003
  BaseFeature = -> PolarPattern001
  Length = 5
  Length2 = 100
  Profile = -> Sketch007
  Type = 1
FEATURE [PartDesign::PolarPattern] PolarPattern002
  Angle = 90
  Axis = -> Z_Axis001
  BaseFeature = -> Pocket003
  Occurrences = 2
  Originals = -> [Pocket003]
  Reversed = true
FEATURE [Sketcher::SketchObject] Sketch008
  FullyConstrained = true
  MapMode = 5
  Placement = pos=(0,0,0) rot=(1,0,0;3.14159rad)
  Support = -> [PolarPattern002]
  sketch-geometry (1):
    g0: Circle CenterX=0 CenterY=0 CenterZ=0 NormalX=0 NormalY=0 NormalZ=1 AngleXU=0 Radius=3.15
  constraints (2):
    c: Coincident(g0,g-1)
    c: Diameter(g0) = 6.3
FEATURE [PartDesign::Pocket] Pocket004
  BaseFeature = -> PolarPattern002
  Length = 5
  Length2 = 100
  Profile = -> Sketch008
  Refine = true
  Type = 1
FEATURE [PartDesign::Body] Body001  label="Body"
  Group = -> [Sketch004,Pad001,Sketch005,Pocket002,Sketch006,Hole001,PolarPattern001,DatumPlane,Sketch007,Pocket003,PolarPattern002,Sketch008,Pocket004]
  Origin = -> Origin001
  Tip = -> Pocket004
FEATURE [PartDesign::CoordinateSystem] LCS_Origin
  AttacherType = Attacher::AttachEngine3D
  MapMode = 2
  Support = -> [X_Axis]
FEATURE [App::FeaturePython] Variables  # WARN: FeaturePython — macro-defined, semantics opaque (R4)
  Type = App::PropertyContainer
FEATURE [App::DocumentObjectGroup] Constraints
FEATURE [App::DocumentObjectGroup] Configurations
FEATURE [PartDesign::CoordinateSystem] LCS_0
  AttacherType = Attacher::AttachEngine3D
  MapMode = 2
  Support = -> [X_Axis002]
FEATURE [PartDesign::CoordinateSystem] LCS_Bottom
  AttacherType = Attacher::AttachEngine3D
  MapMode = 45
  Placement = pos=(0,-4e-16,0) rot=(0,0,1;0rad)
  Support = -> [Pocket004]
FEATURE [PartDesign::CoordinateSystem] LCS_Hole01
  AttacherType = Attacher::AttachEngine3D
  MapMode = 45
  Placement = pos=(7,0,7) rot=(0,1,0;3.14159rad)
  Support = -> [Pocket004]
FEATURE [PartDesign::CoordinateSystem] LCS_Hole02
  AttacherType = Attacher::AttachEngine3D
  MapMode = 45
  Placement = pos=(-7,0,7) rot=(0,1,0;3.14159rad)
  Support = -> [Pocket004]
FEATURE [PartDesign::CoordinateSystem] LCS_Top
  AttacherType = Attacher::AttachEngine3D
  MapMode = 45
  Placement = pos=(1.49e-14,0,7) rot=(0,0,1;0rad)
  Support = -> [Pocket004]
FEATURE [PartDesign::CoordinateSystem] LCS_Hole03
  AttacherType = Attacher::AttachEngine3D
  MapMode = 45
  Placement = pos=(-7.70335,7.70335,10.8452) rot=(0.678591,-0.281096,0.678601;2.59359rad)
  Support = -> [Pocket004]
FEATURE [PartDesign::CoordinateSystem] LCS_Hole04
  AttacherType = Attacher::AttachEngine3D
  AttachmentOffset = pos=(0,0,0) rot=(0,0,1;3.14159rad)
  MapMode = 45
  Placement = pos=(7.70335,7.70335,10.8452) rot=(0.35739,-0.862858,0.35742;1.71778rad)
  Support = -> [Pocket004]
FEATURE [App::Part] ServoCoupler
  Group = -> [LCS_0,Body001,LCS_Bottom,LCS_Hole01,LCS_Hole02,LCS_Top,LCS_Hole03,LCS_Hole04]
  Origin = -> Origin002
FEATURE [App::DocumentObjectGroup] Parts
  Group = -> [ServoCoupler]
FEATURE [App::Link] ServoCoupler001
  AssemblyType = Part::Link
  AttachedBy = #LCS_Bottom
  AttachedTo = Parent Assembly#LCS_Origin
  LinkPlacement = pos=(0,4e-16,0) rot=(0,0,1;0rad)
  LinkedObject = -> ServoCoupler
  Placement = pos=(0,4e-16,0) rot=(0,0,1;0rad)
  SolverId = Asm4EE
  expr: Placement = LCS_Origin.Placement * AttachmentOffset * LCS_Bottom.Placement ^ -1
FEATURE [App::Link] FixedRing
  AssemblyType = Part::Link
  AttachedBy = #LCS_Bottom
  AttachedTo = ServoCoupler001#LCS_Top
  AttachmentOffset = pos=(0,0,1) rot=(0,0,1;0rad)
  LinkPlacement = pos=(1.5e-14,8e-16,8) rot=(0,0,-1;0.785398rad)
  LinkedObject = -> <external FixedRing.FCStd>#FixedRing
  Placement = pos=(1.5e-14,8e-16,8) rot=(0,0,-1;0.785398rad)
  SolverId = Asm4EE
  expr: Placement = ServoCoupler001.Placement * LCS_Top.Placement * AttachmentOffset * FixedRing#LCS_Bottom.Placement ^ -1
FEATURE [App::Part] Assembly
  AssemblyType = Part::Link
  Group = -> [LCS_Origin,Variables,Constraints,Configurations,ServoCoupler001,FixedRing]
  Origin = -> Origin
  Type = Assembly
---- part parts/Shaft.FCStd = doc fcstd_f85f5ca9c8ee ----
FCSTD DOCUMENT  (FreeCAD 0.19R24367 (Git))
Label: Shaft
License: All rights reserved
LicenseURL: http://en.wikipedia.org/wiki/All_rights_reserved
objects: PartDesign::CoordinateSystem×3, App::DocumentObjectGroup×3, App::Part×2, PartDesign::Chamfer×2, App::FeaturePython×1, Sketcher::SketchObject×1, PartDesign::Pad×1, PartDesign::Body×1
note: 11 computed .brp shape members not serialized (recipe doc carries the construction recipe); baked Part::Feature solids carry a one-line shape summary decoded from their .brp

FEATURE [PartDesign::CoordinateSystem] LCS_Origin
  AttacherType = Attacher::AttachEngine3D
  MapMode = 2
  Support = -> [X_Axis]
FEATURE [App::DocumentObjectGroup] Constraints
FEATURE [App::FeaturePython] Variables  # WARN: FeaturePython — macro-defined, semantics opaque (R4)
  Type = App::PropertyContainer
FEATURE [App::DocumentObjectGroup] Configurations
FEATURE [App::Part] Model
  AssemblyType = Part::Link
  Group = -> [LCS_Origin,Constraints,Variables,Configurations]
  Origin = -> Origin
  Type = Assembly
FEATURE [PartDesign::CoordinateSystem] LCS_0
  AttacherType = Attacher::AttachEngine3D
  MapMode = 2
  Support = -> [X_Axis001]
FEATURE [PartDesign::CoordinateSystem] LCS_0001
  AttacherType = Attacher::AttachEngine3D
  MapMode = 2
  Support = -> [X_Axis002]
FEATURE [Sketcher::SketchObject] Sketch
  FullyConstrained = true
  MapMode = 5
  Support = -> [XY_Plane002]
  sketch-geometry (1):
    g0: Circle CenterX=0 CenterY=0 CenterZ=0 NormalX=0 NormalY=0 NormalZ=1 AngleXU=0 Radius=3
  constraints (2):
    c: Coincident(g0,g-1)
    c: Diameter(g0) = 6
FEATURE [PartDesign::Pad] Pad
  Direction = (1,1,1)
  Length = 45
  Length2 = 100
  Profile = -> Sketch
  Type = 0
FEATURE [PartDesign::Chamfer] Chamfer
  Angle = 45
  Base = -> Pad [Edge3]
  BaseFeature = -> Pad
  ChamferType = 0
  FlipDirection = false
  Size = 0.2
  Size2 = 1
  SupportTransform = false
FEATURE [PartDesign::Chamfer] Chamfer001
  Angle = 45
  Base = -> Chamfer [Edge3]
  BaseFeature = -> Chamfer
  ChamferType = 0
  FlipDirection = false
  Size = 0.2
  Size2 = 1
  SupportTransform = false
FEATURE [PartDesign::Body] Body
  Group = -> [LCS_0001,Sketch,Pad,Chamfer,Chamfer001]
  Origin = -> Origin002
  Tip = -> Chamfer001
FEATURE [App::Part] Shaft
  Group = -> [LCS_0,Body]
  Origin = -> Origin001
FEATURE [App::DocumentObjectGroup] Parts
  Group = -> [Shaft]
---- part parts/SteeringKnuckle.FCStd = doc fcstd_47617b843c71 ----
FCSTD DOCUMENT  (FreeCAD 0.19R24367 (Git))
Label: SteeringKnuckle
License: All rights reserved
LicenseURL: http://en.wikipedia.org/wiki/All_rights_reserved
objects: Sketcher::SketchObject×47, PartDesign::Pocket×30, PartDesign::Pad×15, PartDesign::CoordinateSystem×13, PartDesign::Body×4, App::Part×4, PartDesign::PolarPattern×3, PartDesign::Hole×2
note: 161 computed .brp shape members not serialized (recipe doc carries the construction recipe); baked Part::Feature solids carry a one-line shape summary decoded from their .brp

FEATURE [Sketcher::SketchObject] Sketch
  FullyConstrained = true
  MapMode = 5
  Support = -> [XY_Plane]
  sketch-geometry (4):
    g0: LineSegment StartX=-20.5 StartY=11.5 StartZ=0 EndX=40.5 EndY=11.5 EndZ=0
    g1: LineSegment StartX=40.5 StartY=11.5 StartZ=0 EndX=40.5 EndY=-11.5 EndZ=0
    g2: LineSegment StartX=40.5 StartY=-11.5 StartZ=0 EndX=-20.5 EndY=-11.5 EndZ=0
    g3: LineSegment StartX=-20.5 StartY=-11.5 StartZ=0 EndX=-20.5 EndY=11.5 EndZ=0
  constraints (11):
    c: Coincident(g0,g1)
    c: Coincident(g1,g2)
    c: Coincident(g2,g3)
    c: Coincident(g3,g0)
    c: Horizontal(g0)
    c: Horizontal(g2)
    c: Vertical(g1)
    c: Distance(g0) = 61
    c: Distance(g1) = 23
    c: Symmetric(g0,g2,g-1)
    c: DistanceX(g0,g-1) = 20.5
FEATURE [Sketcher::SketchObject] Sketch001
  FullyConstrained = true
  MapMode = 5
  Placement = pos=(0,0,0) rot=(1,0,0;3.14159rad)
  sketch-geometry (4):
    g0: LineSegment StartX=-10.5 StartY=10.2 StartZ=0 EndX=30.5 EndY=10.2 EndZ=0
    g1: LineSegment StartX=30.5 StartY=10.2 StartZ=0 EndX=30.5 EndY=-10.2 EndZ=0
    g2: LineSegment StartX=30.5 StartY=-10.2 StartZ=0 EndX=-10.5 EndY=-10.2 EndZ=0
    g3: LineSegment StartX=-10.5 StartY=-10.2 StartZ=0 EndX=-10.5 EndY=10.2 EndZ=0
  constraints (11):
    c: Coincident(g0,g1)
    c: Coincident(g1,g2)
    c: Coincident(g2,g3)
    c: Coincident(g3,g0)
    c: Horizontal(g0)
    c: Horizontal(g2)
    c: Vertical(g1)
    c: Distance(g0) = 41
    c: Distance(g1) = 20.4
    c: Symmetric(g0,g2,g-1)
    c: DistanceX(g0,g-1) = 10.5
FEATURE [Sketcher::SketchObject] Sketch002
  FullyConstrained = false
  MapMode = 5
  Placement = pos=(0,0,0) rot=(1,0,0;3.14159rad)
  sketch-geometry (4):
    g0: LineSegment StartX=-14.5 StartY=4 StartZ=0 EndX=-10.5 EndY=4 EndZ=0
    g1: LineSegment StartX=-10.5 StartY=4 StartZ=0 EndX=-10.5 EndY=-4 EndZ=0
    g2: LineSegment StartX=-10.5 StartY=-4 StartZ=0 EndX=-14.5 EndY=-4 EndZ=0
    g3: LineSegment StartX=-14.5 StartY=-4 StartZ=0 EndX=-14.5 EndY=4 EndZ=0
  constraints (10):
    c: Coincident(g0,g1)
    c: Coincident(g1,g2)
    c: Coincident(g2,g3)
    c: Coincident(g3,g0)
    c: Horizontal(g0)
    c: Horizontal(g2)
    c: Vertical(g1)
    c: Distance(g0) = 4
    c: Distance(g3) = 8
    c: Symmetric(g0,g2,g-1)
FEATURE [Sketcher::SketchObject] Sketch004
  FullyConstrained = true
  MapMode = 5
  Support = -> [XY_Plane001]
  sketch-geometry (4):
    g0: LineSegment StartX=-20.5 StartY=11.5 StartZ=0 EndX=40.5 EndY=11.5 EndZ=0
    g1: LineSegment StartX=40.5 StartY=11.5 StartZ=0 EndX=40.5 EndY=-11.5 EndZ=0
    g2: LineSegment StartX=40.5 StartY=-11.5 StartZ=0 EndX=-20.5 EndY=-11.5 EndZ=0
    g3: LineSegment StartX=-20.5 StartY=-11.5 StartZ=0 EndX=-20.5 EndY=11.5 EndZ=0
  constraints (11):
    c: Coincident(g0,g1)
    c: Coincident(g1,g2)
    c: Coincident(g2,g3)
    c: Coincident(g3,g0)
    c: Horizontal(g0)
    c: Horizontal(g2)
    c: Vertical(g1)
    c: Distance(g0) = 61
    c: Distance(g1) = 23
    c: Symmetric(g0,g2,g-1)
    c: DistanceX(g0,g-1) = 20.5
FEATURE [Sketcher::SketchObject] Sketch005
  FullyConstrained = true
  MapMode = 5
  sketch-geometry (4):
    g0: LineSegment StartX=-17.5 StartY=10 StartZ=0 EndX=37.5 EndY=10 EndZ=0
    g1: LineSegment StartX=37.5 StartY=10 StartZ=0 EndX=37.5 EndY=-10 EndZ=0
    g2: LineSegment StartX=37.5 StartY=-10 StartZ=0 EndX=-17.5 EndY=-10 EndZ=0
    g3: LineSegment StartX=-17.5 StartY=-10 StartZ=0 EndX=-17.5 EndY=10 EndZ=0
  constraints (11):
    c: Coincident(g0,g1)
    c: Coincident(g1,g2)
    c: Coincident(g2,g3)
    c: Coincident(g3,g0)
    c: Horizontal(g0)
    c: Horizontal(g2)
    c: Vertical(g1)
    c: Distance(g1) = 20
    c: Distance(g0) = 55
    c: Symmetric(g0,g2,g-1)
    c: DistanceX(g0,g-1) = 17.5
FEATURE [Sketcher::SketchObject] Sketch006
  FullyConstrained = true
  MapMode = 5
  Placement = pos=(0,0,-3) rot=(0,0,1;0rad)
  sketch-geometry (4):
    g0: LineSegment StartX=-10 StartY=10 StartZ=0 EndX=30 EndY=10 EndZ=0
    g1: LineSegment StartX=30 StartY=10 StartZ=0 EndX=30 EndY=-10 EndZ=0
    g2: LineSegment StartX=30 StartY=-10 StartZ=0 EndX=-10 EndY=-10 EndZ=0
    g3: LineSegment StartX=-10 StartY=-10 StartZ=0 EndX=-10 EndY=10 EndZ=0
  constraints (11):
    c: Coincident(g0,g1)
    c: Coincident(g1,g2)
    c: Coincident(g2,g3)
    c: Coincident(g3,g0)
    c: Horizontal(g0)
    c: Horizontal(g2)
    c: Vertical(g1)
    c: Distance(g1) = 20
    c: Distance(g0) = 40
    c: Symmetric(g0,g2,g-1)
    c: DistanceX(g0,g-1) = 10
FEATURE [Sketcher::SketchObject] Sketch008
  FullyConstrained = true
  MapMode = 5
  Placement = pos=(0,0,-3) rot=(0,0,1;0rad)
  sketch-geometry (8):
    g0: LineSegment StartX=-17 StartY=1 StartZ=0 EndX=-10 EndY=1 EndZ=0
    g1: LineSegment StartX=-10 StartY=1 StartZ=0 EndX=-10 EndY=-1 EndZ=0
    g2: LineSegment StartX=-10 StartY=-1 StartZ=0 EndX=-17 EndY=-1 EndZ=0
    g3: LineSegment StartX=-17 StartY=-1 StartZ=0 EndX=-17 EndY=1 EndZ=0
    g4: LineSegment StartX=30 StartY=1 StartZ=0 EndX=37 EndY=1 EndZ=0
    g5: LineSegment StartX=37 StartY=1 StartZ=0 EndX=37 EndY=-1 EndZ=0
    g6: LineSegment StartX=37 StartY=-1 StartZ=0 EndX=30 EndY=-1 EndZ=0
    g7: LineSegment StartX=30 StartY=-1 StartZ=0 EndX=30 EndY=1 EndZ=0
  constraints (22):
    c: Coincident(g0,g1)
    c: Coincident(g1,g2)
    c: Coincident(g2,g3)
    c: Coincident(g3,g0)
    c: Horizontal(g0)
    c: Horizontal(g2)
    c: Vertical(g1)
    c: Distance(g1) = 2
    c: Distance(g0) = 7
    c: Symmetric(g0,g2,g-1)
    c: DistanceX(g0,g-1) = 10
    c: Coincident(g4,g5)
    c: Coincident(g5,g6)
    c: Coincident(g6,g7)
    c: Coincident(g7,g4)
    c: Horizontal(g4)
    c: Horizontal(g6)
    c: Vertical(g7)
    c: Distance(g7) = 2
    c: Distance(g4) = 7
    c: Symmetric(g4,g5,g-1)
    c: DistanceX(g-1,g4) = 30
FEATURE [Sketcher::SketchObject] Sketch009
  FullyConstrained = true
  MapMode = 5
  sketch-geometry (1):
    g0: Circle CenterX=0 CenterY=0 CenterZ=0 NormalX=0 NormalY=0 NormalZ=1 AngleXU=0 Radius=24
  constraints (2):
    c: Coincident(g0,g-1)
    c: Diameter(g0) = 48
FEATURE [PartDesign::Pad] Pad002
  Direction = (1,1,1)
  Length = 60
  Length2 = 100
  Profile = -> Sketch009
  Reversed = true
  Type = 0
FEATURE [PartDesign::Pad] Pad003
  BaseFeature = -> Pad002
  Direction = (1,1,1)
  Length = 15
  Length2 = 100
  Profile = -> Sketch004
  Reversed = true
  Type = 0
FEATURE [Sketcher::SketchObject] Sketch015
  FullyConstrained = true
  MapMode = 5
  Placement = pos=(0,0,0) rot=(1,0,0;3.14159rad)
  sketch-geometry (1):
    g0: Circle CenterX=0 CenterY=0 CenterZ=0 NormalX=0 NormalY=0 NormalZ=1 AngleXU=0 Radius=24
  constraints (2):
    c: Coincident(g0,g-1)
    c: Diameter(g0) = 48
FEATURE [PartDesign::Pad] Pad
  Direction = (1,1,1)
  Length = 30
  Length2 = 100
  Profile = -> Sketch
  Refine = true
  Type = 0
FEATURE [PartDesign::Pad] Pad006
  BaseFeature = -> Pad
  Direction = (1,1,1)
  Length = 30
  Length2 = 100
  Profile = -> Sketch015
  Reversed = true
  Type = 0
FEATURE [Sketcher::SketchObject] Sketch019
  FullyConstrained = true
  MapMode = 5
  Placement = pos=(0,0,0) rot=(0.57735,0.57735,0.57735;2.0944rad)
  Support = -> [YZ_Plane]
  sketch-geometry (4):
    g0: LineSegment StartX=-4.5 StartY=25.0833 StartZ=0 EndX=4.5 EndY=25.0833 EndZ=0
    g1: LineSegment StartX=4.5 StartY=25.0833 StartZ=0 EndX=4.5 EndY=21.0833 EndZ=0
    g2: LineSegment StartX=4.5 StartY=21.0833 StartZ=0 EndX=-4.5 EndY=21.0833 EndZ=0
    g3: LineSegment StartX=-4.5 StartY=21.0833 StartZ=0 EndX=-4.5 EndY=25.0833 EndZ=0
  constraints (11):
    c: Coincident(g0,g1)
    c: Coincident(g1,g2)
    c: Coincident(g2,g3)
    c: Coincident(g3,g0)
    c: Horizontal(g2)
    c: Vertical(g1)
    c: Vertical(g3)
    c: Distance(g0) = 9
    c: Symmetric(g0,g0,g-2)
    c: Distance(g1) = 4
    c: DistanceY(g2) = 21.0833
FEATURE [Sketcher::SketchObject] Sketch027
  FullyConstrained = true
  MapMode = 5
  Support = -> [XY_Plane002]
  sketch-geometry (1):
    g0: Circle CenterX=0 CenterY=0 CenterZ=0 NormalX=0 NormalY=0 NormalZ=1 AngleXU=0 Radius=21
  constraints (2):
    c: Coincident(g0,g-1)
    c: Diameter(g0) = 42
FEATURE [PartDesign::Pad] Pad011
  Direction = (1,1,1)
  Length = 30
  Length2 = 100
  Profile = -> Sketch027
  Type = 0
FEATURE [Sketcher::SketchObject] Sketch029
  FullyConstrained = true
  MapMode = 5
  Placement = pos=(0,0,0) rot=(1,0,0;3.14159rad)
  Support = -> [Pad011]
  sketch-geometry (4):
    g0: LineSegment StartX=0 StartY=12.5 StartZ=0 EndX=34 EndY=12.5 EndZ=0
    g1: LineSegment StartX=34 StartY=12.5 StartZ=0 EndX=34 EndY=-12.5 EndZ=0
    g2: LineSegment StartX=34 StartY=-12.5 StartZ=0 EndX=0 EndY=-12.5 EndZ=0
    g3: LineSegment StartX=0 StartY=-12.5 StartZ=0 EndX=0 EndY=12.5 EndZ=0
  constraints (11):
    c: Coincident(g0,g1)
    c: Coincident(g1,g2)
    c: Coincident(g2,g3)
    c: Coincident(g3,g0)
    c: Horizontal(g0)
    c: Horizontal(g2)
    c: Vertical(g1)
    c: PointOnObject(g0,g-2)
    c: Distance(g3) = 25
    c: Distance(g0) = 34
    c: Symmetric(g0,g2,g-1)
FEATURE [PartDesign::Pad] Pad012
  BaseFeature = -> Pad011
  Direction = (1,1,1)
  Length = 25
  Length2 = 100
  Profile = -> Sketch029
  Reversed = true
  Type = 0
FEATURE [Sketcher::SketchObject] Sketch031
  FullyConstrained = true
  MapMode = 5
  Placement = pos=(40,0,0) rot=(0.57735,0.57735,0.57735;2.0944rad)
  sketch-geometry (4):
    g0: LineSegment StartX=-10.5 StartY=23 StartZ=0 EndX=10.5 EndY=23 EndZ=0
    g1: LineSegment StartX=10.5 StartY=23 StartZ=0 EndX=10.5 EndY=2 EndZ=0
    g2: LineSegment StartX=10.5 StartY=2 StartZ=0 EndX=-10.5 EndY=2 EndZ=0
    g3: LineSegment StartX=-10.5 StartY=2 StartZ=0 EndX=-10.5 EndY=23 EndZ=0
  constraints (11):
    c: Coincident(g0,g1)
    c: Coincident(g1,g2)
    c: Coincident(g2,g3)
    c: Coincident(g3,g0)
    c: Horizontal(g0)
    c: Vertical(g1)
    c: Vertical(g3)
    c: Distance(g0) = 21
    c: Equal(g0,g1)
    c: Symmetric(g2,g1,g-2)
    c: DistanceY(g-1,g1) = 2
FEATURE [PartDesign::Pocket] Pocket020
  BaseFeature = -> Pad006
  Length = 5
  Length2 = 100
  Profile = -> Sketch019
  Type = 1
FEATURE [Sketcher::SketchObject] Sketch036
  FullyConstrained = true
  MapMode = 5
  sketch-geometry (4):
    g0: LineSegment StartX=-12.5 StartY=50 StartZ=0 EndX=12.5 EndY=50 EndZ=0
    g1: LineSegment StartX=12.5 StartY=50 StartZ=0 EndX=12.5 EndY=10 EndZ=0
    g2: LineSegment StartX=12.5 StartY=10 StartZ=0 EndX=-12.5 EndY=10 EndZ=0
    g3: LineSegment StartX=-12.5 StartY=10 StartZ=0 EndX=-12.5 EndY=50 EndZ=0
  constraints (11):
    c: Coincident(g0,g1)
    c: Coincident(g1,g2)
    c: Coincident(g2,g3)
    c: Coincident(g3,g0)
    c: Horizontal(g0)
    c: Vertical(g1)
    c: Vertical(g3)
    c: Distance(g0) = 25
    c: Distance(g1) = 40
    c: Symmetric(g2,g1,g-2)
    c: DistanceY(g-1,g2) = 10
FEATURE [PartDesign::Pad] Pad015
  BaseFeature = -> Pad003
  Direction = (1,1,1)
  Length = 25
  Length2 = 100
  Profile = -> Sketch036
  Reversed = true
  Type = 0
FEATURE [Sketcher::SketchObject] Sketch038
  FullyConstrained = true
  MapMode = 5
  sketch-geometry (1):
    g0: Circle CenterX=0 CenterY=0 CenterZ=0 NormalX=0 NormalY=0 NormalZ=1 AngleXU=0 Radius=13
  constraints (2):
    c: Coincident(g0,g-1)
    c: Diameter(g0) = 26
FEATURE [Sketcher::SketchObject] Sketch043
  FullyConstrained = true
  MapMode = 5
  Placement = pos=(0,0,0) rot=(0.57735,0.57735,0.57735;2.0944rad)
  Support = -> [YZ_Plane001]
  sketch-geometry (3):
    g0: LineSegment StartX=23 StartY=-24 StartZ=0 EndX=49 EndY=-24 EndZ=0
    g1: LineSegment StartX=23 StartY=-24 StartZ=0 EndX=23 EndY=-49 EndZ=0
    g2: LineSegment StartX=49 StartY=-24 StartZ=0 EndX=23 EndY=-49 EndZ=0
  constraints (9):
    c: Horizontal(g0)
    c: Coincident(g1,g0)
    c: Vertical(g1)
    c: Coincident(g2,g0)
    c: Coincident(g2,g1)
    c: Distance(g0) = 26
    c: Distance(g1) = 25
    c: DistanceX(g0) = 23
    c: DistanceY(g0) = -24
FEATURE [PartDesign::Pad] Pad016
  BaseFeature = -> Pad015
  Direction = (1,1,1)
  Length = 3
  Length2 = 100
  Midplane = true
  Profile = -> Sketch043
  Type = 0
FEATURE [Sketcher::SketchObject] Sketch047
  FullyConstrained = true
  MapMode = 5
  Support = -> [XY_Plane001]
  sketch-geometry (1):
    g0: Circle CenterX=0 CenterY=0 CenterZ=0 NormalX=0 NormalY=0 NormalZ=1 AngleXU=0 Radius=32
  constraints (2):
    c: Coincident(g0,g-1)
    c: Diameter(g0) = 64
FEATURE [PartDesign::Pad] Pad017
  BaseFeature = -> Pad016
  Direction = (1,1,1)
  Length = 15
  Length2 = 100
  Profile = -> Sketch047
  Reversed = true
  Type = 0
FEATURE [PartDesign::Pocket] Pocket030
  BaseFeature = -> Pad017
  Length = 3
  Length2 = 100
  Profile = -> Sketch005
  Type = 0
FEATURE [PartDesign::Pocket] Pocket031
  BaseFeature = -> Pocket030
  Length = 3
  Length2 = 100
  Profile = -> Sketch008
  Type = 0
FEATURE [PartDesign::Pocket] Pocket032
  BaseFeature = -> Pocket031
  Length = 48
  Length2 = 100
  Profile = -> Sketch038
  Type = 0
FEATURE [PartDesign::Pocket] Pocket033
  BaseFeature = -> Pocket032
  Length = 9
  Length2 = 100
  Profile = -> Sketch006
  Type = 0
FEATURE [Sketcher::SketchObject] Sketch053
  FullyConstrained = true
  MapMode = 5
  Placement = pos=(0,0,-15) rot=(1,0,0;3.14159rad)
  sketch-geometry (2):
    g0: LineSegment StartX=0 StartY=0 StartZ=0 EndX=19.799 EndY=19.799 EndZ=0
    g1: Circle CenterX=19.799 CenterY=19.799 CenterZ=0 NormalX=0 NormalY=0 NormalZ=1 AngleXU=0 Radius=3
  constraints (5):
    c: Coincident(g0,g-1)
    c: Distance(g0) = 28
    c: Angle(g-1,g0) = 0.785398
    c: Coincident(g1,g0)
    c: Diameter(g1) = 6
FEATURE [PartDesign::Hole] Hole
  BaseFeature = -> Pocket033
  Depth = 25
  DepthType = 0
  Diameter = 3
  DrillForDepth = false
  DrillPoint = 1
  DrillPointAngle = 118
  HoleCutCountersinkAngle = 90
  HoleCutCustomValues = false
  HoleCutDepth = 12
  HoleCutDiameter = 6
  HoleCutType = 1
  ModelActualThread = false
  Profile = -> Sketch053
  Tapered = false
  TaperedAngle = 90
  ThreadAngle = 0
  ThreadClass = 0
  ThreadCutOffInner = 0
  ThreadCutOffOuter = 0
  ThreadDirection = 0
  ThreadFit = 0
  ThreadPitch = 0
  ThreadSize = 0
  ThreadType = 0
  Threaded = false
FEATURE [PartDesign::PolarPattern] PolarPattern
  Angle = 360
  Axis = -> Z_Axis001
  BaseFeature = -> Hole
  Occurrences = 4
  Originals = -> [Hole]
FEATURE [Sketcher::SketchObject] Sketch054
  FullyConstrained = true
  MapMode = 5
  Support = -> [XY_Plane]
  sketch-geometry (1):
    g0: Circle CenterX=0 CenterY=0 CenterZ=0 NormalX=0 NormalY=0 NormalZ=1 AngleXU=0 Radius=32
  constraints (2):
    c: Coincident(g0,g-1)
    c: Diameter(g0) = 64
FEATURE [PartDesign::Pad] Pad018
  BaseFeature = -> Pocket020
  Direction = (1,1,1)
  Length = 10
  Length2 = 100
  Profile = -> Sketch054
  Type = 0
FEATURE [PartDesign::Pocket] Pocket
  BaseFeature = -> Pad018
  Length = 29
  Length2 = 100
  Profile = -> Sketch001
  Type = 0
FEATURE [PartDesign::Pocket] Pocket039
  BaseFeature = -> Pocket
  Length = 28
  Length2 = 100
  Profile = -> Sketch002
  Type = 0
FEATURE [Sketcher::SketchObject] Sketch055
  FullyConstrained = true
  MapMode = 5
  Placement = pos=(0,0,0) rot=(1,0,0;3.14159rad)
  Support = -> [Pocket039]
  sketch-geometry (2):
    g0: LineSegment StartX=0 StartY=0 StartZ=0 EndX=19.799 EndY=19.799 EndZ=0
    g1: Circle CenterX=19.799 CenterY=19.799 CenterZ=0 NormalX=0 NormalY=0 NormalZ=1 AngleXU=0 Radius=2.25
  constraints (5):
    c: Coincident(g0,g-1)
    c: Distance(g0) = 28
    c: Angle(g-1,g0) = 0.785398
    c: Coincident(g1,g0)
    c: Diameter(g1) = 4.5
FEATURE [PartDesign::Pocket] Pocket040
  BaseFeature = -> Pocket039
  Length = 8
  Length2 = 100
  Profile = -> Sketch055
  Refine = true
  Type = 1
FEATURE [PartDesign::PolarPattern] PolarPattern001
  Angle = 360
  Axis = -> Z_Axis
  BaseFeature = -> Pocket040
  Occurrences = 4
  Originals = -> [Pocket040]
FEATURE [PartDesign::Body] Body  label="BodyTop"
  Group = -> [Sketch,Sketch001,Sketch002,Sketch015,Pad,Pad006,Sketch019,Pocket020,Sketch054,Pad018,Pocket,Pocket039,Sketch055,Pocket040,PolarPattern001]
  Origin = -> Origin
  Tip = -> PolarPattern001
FEATURE [Sketcher::SketchObject] Sketch056
  FullyConstrained = true
  MapMode = 5
  Placement = pos=(0,0,-48) rot=(0,0,1;0rad)
  Support = -> [PolarPattern]
  sketch-geometry (1):
    g0: Circle CenterX=0 CenterY=0 CenterZ=0 NormalX=0 NormalY=0 NormalZ=1 AngleXU=0 Radius=9.75
  constraints (2):
    c: Coincident(g0,g-1)
    c: Diameter(g0) = 19.5
FEATURE [PartDesign::Pocket] Pocket041
  BaseFeature = -> PolarPattern
  Length = 6
  Length2 = 100
  Profile = -> Sketch056
  Type = 0
FEATURE [Sketcher::SketchObject] Sketch057
  FullyConstrained = true
  MapMode = 5
  Placement = pos=(0,0,-54) rot=(0,0,1;0rad)
  Support = -> [Pocket041]
  sketch-geometry (1):
    g0: Circle CenterX=0 CenterY=0 CenterZ=0 NormalX=0 NormalY=0 NormalZ=1 AngleXU=0 Radius=4.5
  constraints (2):
    c: Coincident(g0,g-1)
    c: Diameter(g0) = 9
FEATURE [PartDesign::Pocket] Pocket042
  BaseFeature = -> Pocket041
  Length = 5
  Length2 = 100
  Profile = -> Sketch057
  Type = 1
FEATURE [Sketcher::SketchObject] Sketch058
  FullyConstrained = true
  MapMode = 5
  Placement = pos=(0,0,-60) rot=(1,0,0;3.14159rad)
  Support = -> [Pocket042]
  sketch-geometry (1):
    g0: Circle CenterX=0 CenterY=0 CenterZ=0 NormalX=0 NormalY=0 NormalZ=1 AngleXU=0 Radius=22
  constraints (2):
    c: Coincident(g0,g-1)
    c: Diameter(g0) = 44
FEATURE [PartDesign::Pocket] Pocket043
  BaseFeature = -> Pocket042
  Length = 2
  Length2 = 100
  Profile = -> Sketch058
  Type = 0
FEATURE [Sketcher::SketchObject] Sketch059
  FullyConstrained = true
  MapMode = 5
  Placement = pos=(0,0,-58) rot=(1,0,0;3.14159rad)
  Support = -> [Pocket043]
  sketch-geometry (1):
    g0: Circle CenterX=0 CenterY=0 CenterZ=0 NormalX=0 NormalY=0 NormalZ=1 AngleXU=0 Radius=6.25
  constraints (2):
    c: Coincident(g0,g-1)
    c: Diameter(g0) = 12.5
FEATURE [PartDesign::Pocket] Pocket044
  BaseFeature = -> Pocket043
  Length = 2
  Length2 = 100
  Profile = -> Sketch059
  Type = 0
FEATURE [Sketcher::SketchObject] Sketch060
  FullyConstrained = true
  MapMode = 5
  Placement = pos=(0,50,0) rot=(0,0.707107,0.707107;3.14159rad)
  Support = -> [Pocket044]
  sketch-geometry (4):
    g0: LineSegment StartX=-10.5 StartY=-2 StartZ=0 EndX=10.5 EndY=-2 EndZ=0
    g1: LineSegment StartX=10.5 StartY=-2 StartZ=0 EndX=10.5 EndY=-23 EndZ=0
    g2: LineSegment StartX=10.5 StartY=-23 StartZ=0 EndX=-10.5 EndY=-23 EndZ=0
    g3: LineSegment StartX=-10.5 StartY=-23 StartZ=0 EndX=-10.5 EndY=-2 EndZ=0
  constraints (11):
    c: Coincident(g0,g1)
    c: Coincident(g1,g2)
    c: Coincident(g2,g3)
    c: Coincident(g3,g0)
    c: Horizontal(g0)
    c: Vertical(g1)
    c: Vertical(g3)
    c: Distance(g0) = 21
    c: Equal(g0,g1)
    c: Symmetric(g2,g1,g-2)
    c: DistanceY(g0,g-1) = 2
FEATURE [PartDesign::Pocket] Pocket045
  BaseFeature = -> Pocket044
  Length = 36
  Length2 = 100
  Profile = -> Sketch060
  Type = 0
FEATURE [Sketcher::SketchObject] Sketch061
  FullyConstrained = true
  MapMode = 5
  Placement = pos=(0,0,0) rot=(1,0,0;3.14159rad)
  Support = -> [Pad012]
  sketch-geometry (1):
    g0: Circle CenterX=0 CenterY=0 CenterZ=0 NormalX=0 NormalY=0 NormalZ=1 AngleXU=0 Radius=6.15
  constraints (2):
    c: Coincident(g0,g-1)
    c: Diameter(g0) = 12.3
FEATURE [PartDesign::Pocket] Pocket046
  BaseFeature = -> Pad012
  Length = 20
  Length2 = 100
  Profile = -> Sketch061
  Type = 0
FEATURE [Sketcher::SketchObject] Sketch062
  FullyConstrained = true
  MapMode = 5
  Placement = pos=(0,0,30) rot=(0,0,1;0rad)
  Support = -> [Pocket046]
  sketch-geometry (1):
    g0: Circle CenterX=0 CenterY=0 CenterZ=0 NormalX=0 NormalY=0 NormalZ=1 AngleXU=0 Radius=3.15
  constraints (2):
    c: Coincident(g0,g-1)
    c: Diameter(g0) = 6.3
FEATURE [PartDesign::Pocket] Pocket047
  BaseFeature = -> Pocket046
  Length = 5
  Length2 = 100
  Profile = -> Sketch062
  Type = 1
FEATURE [PartDesign::Pocket] Pocket048
  BaseFeature = -> Pocket047
  Length = 32
  Length2 = 100
  Profile = -> Sketch031
  Type = 0
FEATURE [Sketcher::SketchObject] Sketch063
  FullyConstrained = true
  MapMode = 5
  Placement = pos=(0,0,0) rot=(1,0,0;1.5708rad)
  Support = -> [XZ_Plane002]
  sketch-geometry (1):
    g0: Circle CenterX=0 CenterY=15 CenterZ=0 NormalX=0 NormalY=0 NormalZ=1 AngleXU=0 Radius=2.25
  constraints (3):
    c: PointOnObject(g0,g-2)
    c: Diameter(g0) = 4.5
    c: DistanceY(g-1,g0) = 15
FEATURE [PartDesign::Pocket] Pocket049
  BaseFeature = -> Pocket048
  Length = 5
  Length2 = 100
  Profile = -> Sketch063
  Type = 1
FEATURE [Sketcher::SketchObject] Sketch064
  FullyConstrained = true
  MapMode = 5
  Placement = pos=(0,0,0) rot=(0.57735,0.57735,0.57735;2.0944rad)
  Support = -> [YZ_Plane002]
  sketch-geometry (1):
    g0: Circle CenterX=0 CenterY=15 CenterZ=0 NormalX=0 NormalY=0 NormalZ=1 AngleXU=0 Radius=2.25
  constraints (3):
    c: PointOnObject(g0,g-2)
    c: DistanceY(g-1,g0) = 15
    c: Diameter(g0) = 4.5
FEATURE [PartDesign::Pocket] Pocket050
  BaseFeature = -> Pocket049
  Length = 5
  Length2 = 100
  Profile = -> Sketch064
  Type = 1
FEATURE [Sketcher::SketchObject] Sketch065
  FullyConstrained = true
  MapMode = 5
  Support = -> [Pocket045]
  sketch-geometry (3):
    g0: LineSegment StartX=-6 StartY=40 StartZ=0 EndX=6 EndY=40 EndZ=0
    g1: Circle CenterX=-6 CenterY=40 CenterZ=0 NormalX=0 NormalY=0 NormalZ=1 AngleXU=0 Radius=2.15
    g2: Circle CenterX=6 CenterY=40 CenterZ=0 NormalX=0 NormalY=0 NormalZ=1 AngleXU=0 Radius=2.15
  constraints (7):
    c: Symmetric(g0,g0,g-2)
    c: Distance(g0) = 12
    c: DistanceY(g-1,g0) = 40
    c: Coincident(g1,g0)
    c: Coincident(g2,g0)
    c: Diameter(g1) = 4.3
    c: Diameter(g2) = 4.3
FEATURE [PartDesign::Pocket] Pocket051
  BaseFeature = -> Pocket045
  Length = 5
  Length2 = 100
  Profile = -> Sketch065
  Refine = true
  Type = 1
FEATURE [PartDesign::Body] Body001  label="BottomL"
  Group = -> [Sketch004,Sketch005,Sketch006,Sketch008,Sketch009,Pad002,Pad003,Sketch036,Pad015,Sketch038,Sketch043,Pad016,Sketch047,Pad017,Pocket030,Pocket031,Pocket032,Pocket033,Sketch053,Hole,PolarPattern,Sketch056,Pocket041,Sketch057,Pocket042,Sketch058,Pocket043,Sketch059,Pocket044,Sketch060,Pocket045,Sketch065,Pocket051]
  Origin = -> Origin001
  Tip = -> Pocket051
FEATURE [Sketcher::SketchObject] Sketch070
  FullyConstrained = true
  MapMode = 5
  sketch-geometry (3):
    g0: LineSegment StartX=-6 StartY=-40 StartZ=0 EndX=6 EndY=-40 EndZ=0
    g1: Circle CenterX=-6 CenterY=-40 CenterZ=0 NormalX=0 NormalY=0 NormalZ=1 AngleXU=0 Radius=2.15
    g2: Circle CenterX=6 CenterY=-40 CenterZ=0 NormalX=0 NormalY=0 NormalZ=1 AngleXU=0 Radius=2.15
  constraints (7):
    c: Symmetric(g0,g0,g-2)
    c: Distance(g0) = 12
    c: Coincident(g1,g0)
    c: Coincident(g2,g0)
    c: Diameter(g1) = 4.3
    c: Diameter(g2) = 4.3
    c: DistanceY(g1,g-1) = 40
FEATURE [Sketcher::SketchObject] Sketch071
  FullyConstrained = true
  MapMode = 5
  Placement = pos=(0,0,-15) rot=(1,0,0;3.14159rad)
  sketch-geometry (2):
    g0: LineSegment StartX=0 StartY=0 StartZ=0 EndX=19.799 EndY=19.799 EndZ=0
    g1: Circle CenterX=19.799 CenterY=19.799 CenterZ=0 NormalX=0 NormalY=0 NormalZ=1 AngleXU=0 Radius=3
  constraints (5):
    c: Coincident(g0,g-1)
    c: Distance(g0) = 28
    c: Angle(g-1,g0) = 0.785398
    c: Coincident(g1,g0)
    c: Diameter(g1) = 6
FEATURE [Sketcher::SketchObject] Sketch084
  FullyConstrained = true
  MapMode = 5
  Placement = pos=(0,0,-3) rot=(0,0,1;0rad)
  sketch-geometry (4):
    g0: LineSegment StartX=-10 StartY=10 StartZ=0 EndX=30 EndY=10 EndZ=0
    g1: LineSegment StartX=30 StartY=10 StartZ=0 EndX=30 EndY=-10 EndZ=0
    g2: LineSegment StartX=30 StartY=-10 StartZ=0 EndX=-10 EndY=-10 EndZ=0
    g3: LineSegment StartX=-10 StartY=-10 StartZ=0 EndX=-10 EndY=10 EndZ=0
  constraints (11):
    c: Coincident(g0,g1)
    c: Coincident(g1,g2)
    c: Coincident(g2,g3)
    c: Coincident(g3,g0)
    c: Horizontal(g0)
    c: Horizontal(g2)
    c: Vertical(g1)
    c: Distance(g1) = 20
    c: Distance(g0) = 40
    c: Symmetric(g0,g2,g-1)
    c: DistanceX(g0,g-1) = 10
FEATURE [Sketcher::SketchObject] Sketch072
  FullyConstrained = true
  MapMode = 5
  sketch-geometry (1):
    g0: Circle CenterX=0 CenterY=0 CenterZ=0 NormalX=0 NormalY=0 NormalZ=1 AngleXU=0 Radius=13
  constraints (2):
    c: Coincident(g0,g-1)
    c: Diameter(g0) = 26
FEATURE [Sketcher::SketchObject] Sketch083
  FullyConstrained = true
  MapMode = 5
  Placement = pos=(0,0,-3) rot=(0,0,1;0rad)
  sketch-geometry (8):
    g0: LineSegment StartX=-17 StartY=1 StartZ=0 EndX=-10 EndY=1 EndZ=0
    g1: LineSegment StartX=-10 StartY=1 StartZ=0 EndX=-10 EndY=-1 EndZ=0
    g2: LineSegment StartX=-10 StartY=-1 StartZ=0 EndX=-17 EndY=-1 EndZ=0
    g3: LineSegment StartX=-17 StartY=-1 StartZ=0 EndX=-17 EndY=1 EndZ=0
    g4: LineSegment StartX=30 StartY=1 StartZ=0 EndX=37 EndY=1 EndZ=0
    g5: LineSegment StartX=37 StartY=1 StartZ=0 EndX=37 EndY=-1 EndZ=0
    g6: LineSegment StartX=37 StartY=-1 StartZ=0 EndX=30 EndY=-1 EndZ=0
    g7: LineSegment StartX=30 StartY=-1 StartZ=0 EndX=30 EndY=1 EndZ=0
  constraints (22):
    c: Coincident(g0,g1)
    c: Coincident(g1,g2)
    c: Coincident(g2,g3)
    c: Coincident(g3,g0)
    c: Horizontal(g0)
    c: Horizontal(g2)
    c: Vertical(g1)
    c: Distance(g1) = 2
    c: Distance(g0) = 7
    c: Symmetric(g0,g2,g-1)
    c: DistanceX(g0,g-1) = 10
    c: Coincident(g4,g5)
    c: Coincident(g5,g6)
    c: Coincident(g6,g7)
    c: Coincident(g7,g4)
    c: Horizontal(g4)
    c: Horizontal(g6)
    c: Vertical(g7)
    c: Distance(g7) = 2
    c: Distance(g4) = 7
    c: Symmetric(g4,g5,g-1)
    c: DistanceX(g-1,g4) = 30
FEATURE [Sketcher::SketchObject] Sketch082
  FullyConstrained = true
  MapMode = 5
  sketch-geometry (4):
    g0: LineSegment StartX=-17.5 StartY=10 StartZ=0 EndX=37.5 EndY=10 EndZ=0
    g1: LineSegment StartX=37.5 StartY=10 StartZ=0 EndX=37.5 EndY=-10 EndZ=0
    g2: LineSegment StartX=37.5 StartY=-10 StartZ=0 EndX=-17.5 EndY=-10 EndZ=0
    g3: LineSegment StartX=-17.5 StartY=-10 StartZ=0 EndX=-17.5 EndY=10 EndZ=0
  constraints (11):
    c: Coincident(g0,g1)
    c: Coincident(g1,g2)
    c: Coincident(g2,g3)
    c: Coincident(g3,g0)
    c: Horizontal(g0)
    c: Horizontal(g2)
    c: Vertical(g1)
    c: Distance(g1) = 20
    c: Distance(g0) = 55
    c: Symmetric(g0,g2,g-1)
    c: DistanceX(g0,g-1) = 17.5
FEATURE [Sketcher::SketchObject] Sketch075
  FullyConstrained = true
  MapMode = 5
  Support = -> [XY_Plane004]
  sketch-geometry (1):
    g0: Circle CenterX=0 CenterY=0 CenterZ=0 NormalX=0 NormalY=0 NormalZ=1 AngleXU=0 Radius=32
  constraints (2):
    c: Coincident(g0,g-1)
    c: Diameter(g0) = 64
FEATURE [Sketcher::SketchObject] Sketch073
  FullyConstrained = true
  MapMode = 5
  Placement = pos=(0,0,0) rot=(0.57735,0.57735,0.57735;2.0944rad)
  Support = -> [YZ_Plane004]
  sketch-geometry (3):
    g0: LineSegment StartX=-49 StartY=-24 StartZ=0 EndX=-23 EndY=-24 EndZ=0
    g1: LineSegment StartX=-23 StartY=-24 StartZ=0 EndX=-23 EndY=-49 EndZ=0
    g2: LineSegment StartX=-49 StartY=-24 StartZ=0 EndX=-23 EndY=-49 EndZ=0
  constraints (9):
    c: Horizontal(g0)
    c: Coincident(g1,g0)
    c: Vertical(g1)
    c: Coincident(g2,g0)
    c: Coincident(g2,g1)
    c: Distance(g0) = 26
    c: Distance(g1) = 25
    c: DistanceY(g0,g-1) = 24
    c: DistanceX(g0,g-1) = 23
FEATURE [Sketcher::SketchObject] Sketch079
  FullyConstrained = true
  MapMode = 5
  sketch-geometry (4):
    g0: LineSegment StartX=-12.5 StartY=-10 StartZ=0 EndX=12.5 EndY=-10 EndZ=0
    g1: LineSegment StartX=12.5 StartY=-10 StartZ=0 EndX=12.5 EndY=-50 EndZ=0
    g2: LineSegment StartX=12.5 StartY=-50 StartZ=0 EndX=-12.5 EndY=-50 EndZ=0
    g3: LineSegment StartX=-12.5 StartY=-50 StartZ=0 EndX=-12.5 EndY=-10 EndZ=0
  constraints (11):
    c: Coincident(g0,g1)
    c: Coincident(g1,g2)
    c: Coincident(g2,g3)
    c: Coincident(g3,g0)
    c: Horizontal(g0)
    c: Vertical(g1)
    c: Vertical(g3)
    c: Distance(g0) = 25
    c: Distance(g1) = 40
    c: Symmetric(g2,g1,g-2)
    c: DistanceY(g0,g-1) = 10
FEATURE [Sketcher::SketchObject] Sketch081
  FullyConstrained = true
  MapMode = 5
  Support = -> [XY_Plane004]
  sketch-geometry (4):
    g0: LineSegment StartX=-20.5 StartY=11.5 StartZ=0 EndX=40.5 EndY=11.5 EndZ=0
    g1: LineSegment StartX=40.5 StartY=11.5 StartZ=0 EndX=40.5 EndY=-11.5 EndZ=0
    g2: LineSegment StartX=40.5 StartY=-11.5 StartZ=0 EndX=-20.5 EndY=-11.5 EndZ=0
    g3: LineSegment StartX=-20.5 StartY=-11.5 StartZ=0 EndX=-20.5 EndY=11.5 EndZ=0
  constraints (11):
    c: Coincident(g0,g1)
    c: Coincident(g1,g2)
    c: Coincident(g2,g3)
    c: Coincident(g3,g0)
    c: Horizontal(g0)
    c: Horizontal(g2)
    c: Vertical(g1)
    c: Distance(g0) = 61
    c: Distance(g1) = 23
    c: Symmetric(g0,g2,g-1)
    c: DistanceX(g0,g-1) = 20.5
FEATURE [Sketcher::SketchObject] Sketch077
  FullyConstrained = true
  MapMode = 5
  sketch-geometry (1):
    g0: Circle CenterX=0 CenterY=0 CenterZ=0 NormalX=0 NormalY=0 NormalZ=1 AngleXU=0 Radius=24
  constraints (2):
    c: Coincident(g0,g-1)
    c: Diameter(g0) = 48
FEATURE [PartDesign::Pad] Pad019
  Direction = (1,1,1)
  Length = 60
  Length2 = 100
  Profile = -> Sketch077
  Reversed = true
  Type = 0
FEATURE [PartDesign::Pad] Pad020
  BaseFeature = -> Pad019
  Direction = (1,1,1)
  Length = 15
  Length2 = 100
  Profile = -> Sketch081
  Reversed = true
  Type = 0
FEATURE [PartDesign::Pad] Pad021
  BaseFeature = -> Pad020
  Direction = (1,1,1)
  Length = 25
  Length2 = 100
  Profile = -> Sketch079
  Reversed = true
  Type = 0
FEATURE [PartDesign::Pad] Pad022
  BaseFeature = -> Pad021
  Direction = (1,1,1)
  Length = 3
  Length2 = 100
  Midplane = true
  Profile = -> Sketch073
  Type = 0
FEATURE [PartDesign::Pad] Pad023
  BaseFeature = -> Pad022
  Direction = (1,1,1)
  Length = 15
  Length2 = 100
  Profile = -> Sketch075
  Reversed = true
  Type = 0
FEATURE [PartDesign::Pocket] Pocket059
  BaseFeature = -> Pad023
  Length = 3
  Length2 = 100
  Profile = -> Sketch082
  Type = 0
FEATURE [PartDesign::Pocket] Pocket058
  BaseFeature = -> Pocket059
  Length = 3
  Length2 = 100
  Profile = -> Sketch083
  Type = 0
FEATURE [PartDesign::Pocket] Pocket056
  BaseFeature = -> Pocket058
  Length = 48
  Length2 = 100
  Profile = -> Sketch072
  Type = 0
FEATURE [PartDesign::Pocket] Pocket057
  BaseFeature = -> Pocket056
  Length = 9
  Length2 = 100
  Profile = -> Sketch084
  Type = 0
FEATURE [PartDesign::Hole] Hole001
  BaseFeature = -> Pocket057
  Depth = 25
  DepthType = 0
  Diameter = 3
  DrillForDepth = false
  DrillPoint = 1
  DrillPointAngle = 118
  HoleCutCountersinkAngle = 90
  HoleCutCustomValues = false
  HoleCutDepth = 12
  HoleCutDiameter = 6
  HoleCutType = 1
  ModelActualThread = false
  Profile = -> Sketch071
  Tapered = false
  TaperedAngle = 90
  ThreadAngle = 0
  ThreadClass = 0
  ThreadCutOffInner = 0
  ThreadCutOffOuter = 0
  ThreadDirection = 0
  ThreadFit = 0
  ThreadPitch = 0
  ThreadSize = 0
  ThreadType = 0
  Threaded = false
FEATURE [PartDesign::PolarPattern] PolarPattern002
  Angle = 360
  Axis = -> Z_Axis004
  BaseFeature = -> Hole001
  Occurrences = 4
  Originals = -> [Hole001]
FEATURE [PartDesign::Pocket] Pocket061
  BaseFeature = -> PolarPattern002
  Length = 5
  Length2 = 100
  Profile = -> Sketch070
  Type = 1
FEATURE [Sketcher::SketchObject] Sketch078
  FullyConstrained = true
  MapMode = 5
  Placement = pos=(0,-50,0) rot=(1,0,0;1.5708rad)
  Support = -> [Pocket061]
  sketch-geometry (4):
    g0: LineSegment StartX=-10.5 StartY=-2 StartZ=0 EndX=10.5 EndY=-2 EndZ=0
    g1: LineSegment StartX=10.5 StartY=-2 StartZ=0 EndX=10.5 EndY=-23 EndZ=0
    g2: LineSegment StartX=10.5 StartY=-23 StartZ=0 EndX=-10.5 EndY=-23 EndZ=0
    g3: LineSegment StartX=-10.5 StartY=-23 StartZ=0 EndX=-10.5 EndY=-2 EndZ=0
  constraints (11):
    c: Coincident(g0,g1)
    c: Coincident(g1,g2)
    c: Coincident(g2,g3)
    c: Coincident(g3,g0)
    c: Horizontal(g2)
    c: Vertical(g1)
    c: Vertical(g3)
    c: Symmetric(g0,g0,g-2)
    c: Equal(g0,g1)
    c: Distance(g0) = 21
    c: DistanceY(g0,g-1) = 2
FEATURE [PartDesign::Pocket] Pocket065
  BaseFeature = -> Pocket061
  Length = 36
  Length2 = 100
  Profile = -> Sketch078
  Type = 0
FEATURE [Sketcher::SketchObject] Sketch085
  FullyConstrained = true
  MapMode = 5
  Placement = pos=(0,0,-48) rot=(0,0,1;0rad)
  Support = -> [Pocket065]
  sketch-geometry (1):
    g0: Circle CenterX=0 CenterY=0 CenterZ=0 NormalX=0 NormalY=0 NormalZ=1 AngleXU=0 Radius=9.75
  constraints (2):
    c: Coincident(g0,g-1)
    c: Diameter(g0) = 19.5
FEATURE [PartDesign::Pocket] Pocket063
  BaseFeature = -> Pocket065
  Length = 6
  Length2 = 100
  Profile = -> Sketch085
  Type = 0
FEATURE [Sketcher::SketchObject] Sketch076
  FullyConstrained = true
  MapMode = 5
  Placement = pos=(0,0,-54) rot=(0,0,1;0rad)
  Support = -> [Pocket063]
  sketch-geometry (1):
    g0: Circle CenterX=0 CenterY=0 CenterZ=0 NormalX=0 NormalY=0 NormalZ=1 AngleXU=0 Radius=4.5
  constraints (2):
    c: Coincident(g0,g-1)
    c: Diameter(g0) = 9
FEATURE [PartDesign::Pocket] Pocket064
  BaseFeature = -> Pocket063
  Length = 5
  Length2 = 100
  Profile = -> Sketch076
  Type = 1
FEATURE [Sketcher::SketchObject] Sketch080
  FullyConstrained = true
  MapMode = 5
  Placement = pos=(0,0,-60) rot=(1,0,0;3.14159rad)
  Support = -> [Pocket064]
  sketch-geometry (1):
    g0: Circle CenterX=0 CenterY=0 CenterZ=0 NormalX=0 NormalY=0 NormalZ=1 AngleXU=0 Radius=22
  constraints (2):
    c: Coincident(g0,g-1)
    c: Diameter(g0) = 44
FEATURE [PartDesign::Pocket] Pocket060
  BaseFeature = -> Pocket064
  Length = 2
  Length2 = 100
  Profile = -> Sketch080
  Type = 0
FEATURE [Sketcher::SketchObject] Sketch074
  FullyConstrained = true
  MapMode = 5
  Placement = pos=(0,0,-58) rot=(1,0,0;3.14159rad)
  Support = -> [Pocket060]
  sketch-geometry (1):
    g0: Circle CenterX=0 CenterY=0 CenterZ=0 NormalX=0 NormalY=0 NormalZ=1 AngleXU=0 Radius=6.25
  constraints (2):
    c: Coincident(g0,g-1)
    c: Diameter(g0) = 12.5
FEATURE [PartDesign::Pocket] Pocket062
  BaseFeature = -> Pocket060
  Length = 2
  Length2 = 100
  Profile = -> Sketch074
  Type = 0
FEATURE [PartDesign::Body] Body004  label="BottomR"
  Group = -> [Sketch081,Sketch082,Sketch084,Sketch083,Sketch077,Pad019,Pad020,Sketch079,Pad021,Sketch072,Sketch073,Pad022,Sketch075,Pad023,Pocket059,Pocket058,Pocket056,Pocket057,Sketch071,Hole001,PolarPattern002,Sketch070,Pocket061,Sketch078,Pocket065,Sketch085,Pocket063,Sketch076,Pocket064,Sketch080,Pocket060,Sketch074,Pocket062]
  Origin = -> Origin004
  Tip = -> Pocket062
FEATURE [Sketcher::SketchObject] Sketch086
  ExternalGeometry = -> [Pocket050]
  FullyConstrained = true
  MapMode = 5
  Placement = pos=(0,0,0) rot=(1,0,0;3.14159rad)
  Support = -> [Pocket050]
  sketch-geometry (3):
    g0: LineSegment StartX=27 StartY=6 StartZ=0 EndX=27 EndY=-6 EndZ=0
    g1: Circle CenterX=27 CenterY=6 CenterZ=0 NormalX=0 NormalY=0 NormalZ=1 AngleXU=0 Radius=2.15
    g2: Circle CenterX=27 CenterY=-6 CenterZ=0 NormalX=0 NormalY=0 NormalZ=1 AngleXU=0 Radius=2.15
  constraints (7):
    c: Symmetric(g0,g0,g-1)
    c: Distance(g0) = 12
    c: DistanceX(g0,g-3) = 7
    c: Coincident(g1,g0)
    c: Coincident(g2,g0)
    c: Diameter(g1) = 4.3
    c: Diameter(g2) = 4.3
FEATURE [PartDesign::Pocket] Pocket066
  BaseFeature = -> Pocket050
  Length = 5
  Length2 = 100
  Profile = -> Sketch086
  Refine = true
  Type = 1
FEATURE [PartDesign::Body] Body002  label="BodyStator"
  Group = -> [Sketch027,Pad011,Sketch029,Pad012,Sketch031,Sketch061,Pocket046,Sketch062,Pocket047,Pocket048,Sketch063,Pocket049,Sketch064,Pocket050,Sketch086,Pocket066]
  Origin = -> Origin002
  Tip = -> Pocket066
FEATURE [PartDesign::CoordinateSystem] LCS_0
  AttacherType = Attacher::AttachEngine3D
  MapMode = 2
  Support = -> [X_Axis005]
FEATURE [PartDesign::CoordinateSystem] LCS_0001
  AttacherType = Attacher::AttachEngine3D
  MapMode = 2
  Support = -> [X_Axis006]
FEATURE [PartDesign::CoordinateSystem] LCS_0002
  AttacherType = Attacher::AttachEngine3D
  MapMode = 2
  Support = -> [X_Axis007]
FEATURE [App::Part] SteeringKnuckleBottomR
  Group = -> [LCS_0002,Body004]
  Origin = -> Origin007
FEATURE [PartDesign::CoordinateSystem] LCS_0003
  AttacherType = Attacher::AttachEngine3D
  MapMode = 2
  Support = -> [X_Axis008]
FEATURE [App::Part] SteeringKnuckleStator
  Group = -> [LCS_0003,Body002]
  Origin = -> Origin008
FEATURE [PartDesign::CoordinateSystem] LCS_1
  AttacherType = Attacher::AttachEngine3D
  MapMode = 5
  Placement = pos=(0,0,0) rot=(1,0,0;3.14159rad)
  Support = -> [PolarPattern001]
FEATURE [App::Part] SteeringKnuckleTop
  Group = -> [LCS_0,Body,LCS_1]
  Origin = -> Origin005
FEATURE [PartDesign::CoordinateSystem] LCS_2
  AttacherType = Attacher::AttachEngine3D
  MapMode = 5
  Placement = pos=(0,0,-3) rot=(0,1,0;3.14159rad)
  Support = -> [Pocket051]
FEATURE [PartDesign::CoordinateSystem] LCS_3
  AttacherType = Attacher::AttachEngine3D
  MapMode = 5
  Placement = pos=(0,0,0) rot=(0,1,0;3.14159rad)
  Support = -> [Pocket051]
FEATURE [PartDesign::CoordinateSystem] LCS_Screw01
  AttacherType = Attacher::AttachEngine3D
  MapMode = 45
  Placement = pos=(-19.799,19.799,-3) rot=(0,0,1;0rad)
  Support = -> [Pocket051]
FEATURE [PartDesign::CoordinateSystem] LCS_Screw02
  AttacherType = Attacher::AttachEngine3D
  MapMode = 45
  Placement = pos=(-19.799,-19.799,-3) rot=(0,0,1;0rad)
  Support = -> [Pocket051]
FEATURE [PartDesign::CoordinateSystem] LCS_Screw03
  AttacherType = Attacher::AttachEngine3D
  MapMode = 45
  Placement = pos=(19.799,-19.799,-3) rot=(0,0,1;0rad)
  Support = -> [Pocket051]
FEATURE [PartDesign::CoordinateSystem] LCS_Screw04
  AttacherType = Attacher::AttachEngine3D
  MapMode = 45
  Placement = pos=(19.799,19.799,-3) rot=(0,0,1;0rad)
  Support = -> [Pocket051]
FEATURE [PartDesign::CoordinateSystem] LCS_BallBearing
  AttacherType = Attacher::AttachEngine3D
  MapMode = 45
  Placement = pos=(0,-7e-16,-54) rot=(0,1,0;3.14159rad)
  Support = -> [Pocket051]
FEATURE [PartDesign::CoordinateSystem] LCS_SurfaceBearing
  AttacherType = Attacher::AttachEngine3D
  MapMode = 45
  Placement = pos=(2.13e-14,2e-16,-56) rot=(0,1,0;3.14159rad)
  Support = -> [Pocket051]
FEATURE [App::Part] SteeringKnuckleBottomL
  Group = -> [LCS_0001,Body001,LCS_2,LCS_3,LCS_Screw01,LCS_Screw02,LCS_Screw03,LCS_Screw04,LCS_BallBearing,LCS_SurfaceBearing]
  Origin = -> Origin006
